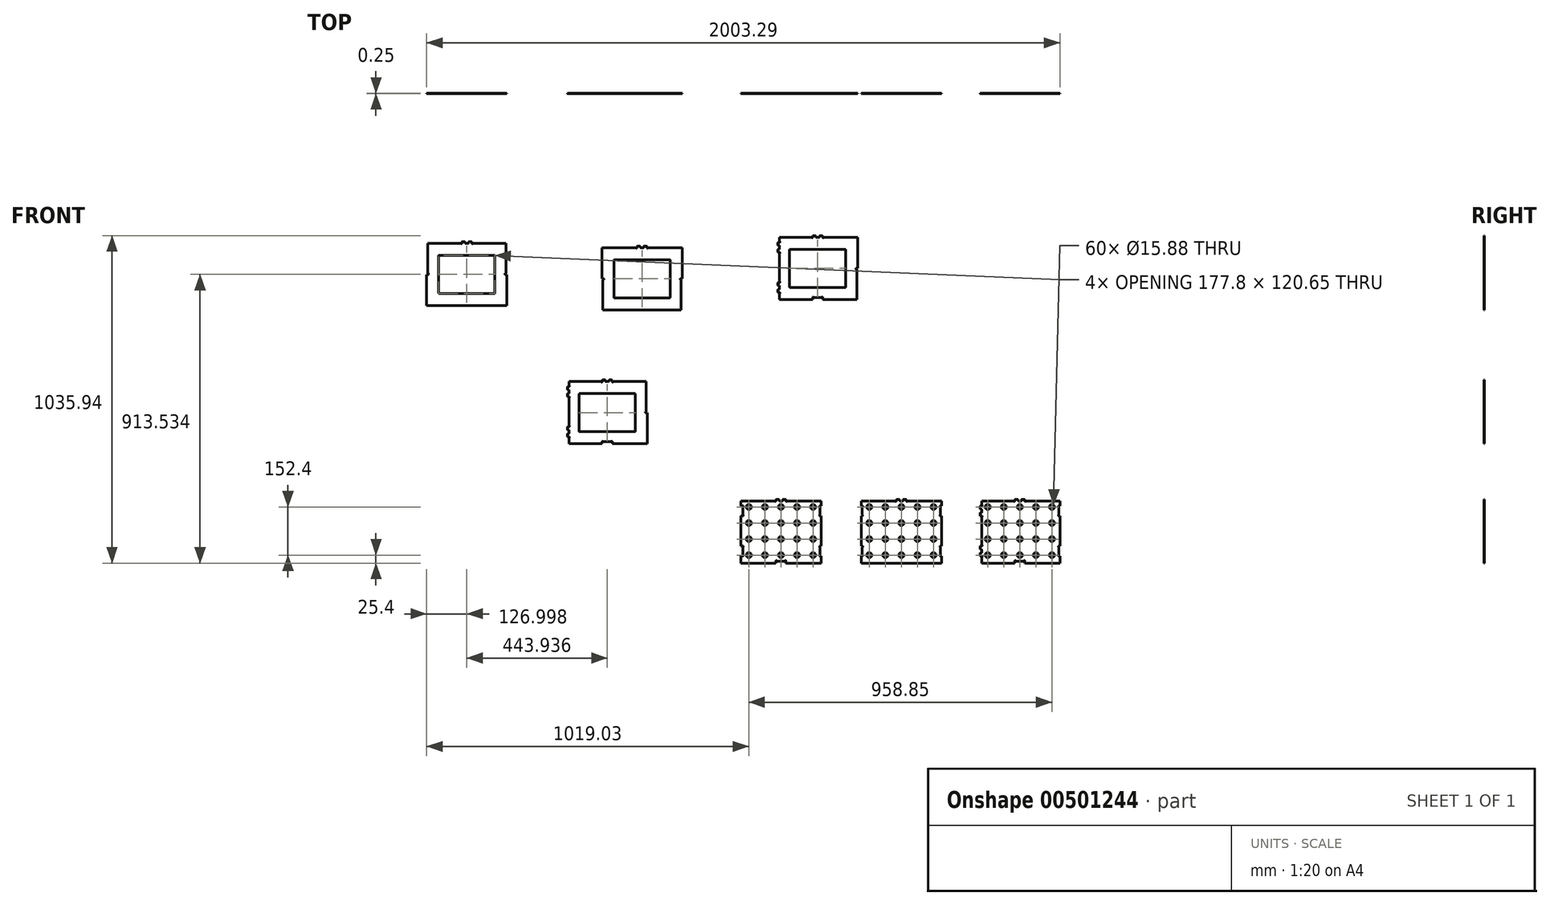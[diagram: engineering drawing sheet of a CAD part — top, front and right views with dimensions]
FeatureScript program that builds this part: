
annotation { "Feature Type Name" : "Feature", "Feature Type Description" : "" }
export const myFeature = defineFeature(function(context is Context, id is Id, definition is map)
    precondition{}
    {
        {
            assignVariable(context, id + "F0", {"name" : "TopPlateThickness", "anyValue" : 0.25});
        }
        {
            assignVariable(context, id + "F1", {"name" : "XMemberThickness", "anyValue" : 0.25});
        }
        {
            var Q0;
            Q0=qCreatedBy(makeId("Front.planeOp"),FACE);
            var sketch = newSketch(context, id + "F2", { "sketchPlane" : qUnion([Q0])});
            skLineSegment(sketch, "E0.MirrorCS", {"start": v(-827.8, -356.83) * mm, "end": v(-827.7, -363.3) * mm});
            skLineSegment(sketch, "E1", {"start": v(-795.8, -356.31) * mm, "end": v(-795.7, -362.8) * mm});
            skArc(sketch, "E2", {"start": v(-824.86, -355.99) * mm, "mid": v(-826.66, -355.28) * mm, "end": v(-827.8, -356.83) * mm});
            skArc(sketch, "E3", {"start": v(-824.86, -355.99) * mm, "mid": v(-824.27, -356.56) * mm, "end": v(-823.47, -356.76) * mm});
            skArc(sketch, "E4.MirrorCS", {"start": v(-798.78, -355.57) * mm, "mid": v(-797, -354.8) * mm, "end": v(-795.8, -356.31) * mm});
            skArc(sketch, "E5.MirrorCS", {"start": v(-798.78, -355.57) * mm, "mid": v(-799.35, -356.16) * mm, "end": v(-800.15, -356.38) * mm});
            skLineSegment(sketch, "E6.trimOffspring", {"start": v(-800.15, -356.38) * mm, "end": v(-823.47, -356.76) * mm});
            skLineSegment(sketch, "E7", {"start": v(-827.8, -356.83) * mm, "end": v(-823.47, -356.76) * mm, "construction": true});
            skLineSegment(sketch, "E8", {"start": v(-800.15, -356.38) * mm, "end": v(-795.8, -356.31) * mm, "construction": true});
            skLineSegment(sketch, "E9", {"start": v(-811.8, -356.57) * mm, "end": v(-811.7, -363.05) * mm, "construction": true});
            skLineSegment(sketch, "E10", {"start": v(-827.7, -363.3) * mm, "end": v(-811.7, -363.05) * mm, "construction": true});
            skLineSegment(sketch, "E11.left", {"start": v(-825.35, -397.01) * mm, "end": v(-825.13, -400.5) * mm});
            skLineSegment(sketch, "E12", {"start": v(-823.86, -395.33) * mm, "end": v(-817.27, -394.91) * mm});
            skArc(sketch, "E13.filletArc", {"start": v(-823.86, -395.33) * mm, "mid": v(-824.96, -395.86) * mm, "end": v(-825.35, -397.01) * mm});
            skLineSegment(sketch, "E14", {"start": v(-813.79, -399.78) * mm, "end": v(-809.54, -399.51) * mm});
            skLineSegment(sketch, "E15.MirrorCS", {"start": v(-794.17, -395.05) * mm, "end": v(-793.95, -398.53) * mm});
            skLineSegment(sketch, "E16.MirrorCS", {"start": v(-795.85, -393.56) * mm, "end": v(-802.44, -393.98) * mm});
            skArc(sketch, "E17.MirrorCS", {"start": v(-795.85, -393.56) * mm, "mid": v(-794.7, -393.96) * mm, "end": v(-794.17, -395.05) * mm});
            skArc(sketch, "E18", {"start": v(-815.59, -396.4) * mm, "mid": v(-816.12, -395.3) * mm, "end": v(-817.27, -394.91) * mm});
            skArc(sketch, "E19", {"start": v(-815.47, -398.3) * mm, "mid": v(-814.93, -399.39) * mm, "end": v(-813.79, -399.78) * mm});
            skArc(sketch, "E20", {"start": v(-805.3, -399.25) * mm, "mid": v(-804.2, -398.71) * mm, "end": v(-803.8, -397.56) * mm});
            skArc(sketch, "E21", {"start": v(-802.44, -393.98) * mm, "mid": v(-803.53, -394.51) * mm, "end": v(-803.93, -395.66) * mm});
            skLineSegment(sketch, "E22", {"start": v(-805.3, -399.25) * mm, "end": v(-809.54, -399.51) * mm});
            skArc(sketch, "E23", {"start": v(-828.3, -400.7) * mm, "mid": v(-826.61, -402.18) * mm, "end": v(-825.13, -400.5) * mm});
            skArc(sketch, "E24", {"start": v(-793.95, -398.53) * mm, "mid": v(-792.27, -400.02) * mm, "end": v(-790.78, -398.33) * mm});
            skLineSegment(sketch, "E25.0", {"start": v(-825.13, -400.5) * mm, "end": v(-793.95, -398.53) * mm, "construction": true});
            skLineSegment(sketch, "E26.0", {"start": v(-817.17, -396.5) * mm, "end": v(-802.34, -395.56) * mm, "construction": true});
            skLineSegment(sketch, "E27.0", {"start": v(-823.86, -395.33) * mm, "end": v(-795.85, -393.56) * mm, "construction": true});
            skLineSegment(sketch, "E28", {"start": v(-823.86, -395.33) * mm, "end": v(-823.55, -400.4) * mm, "construction": true});
            skLineSegment(sketch, "E29", {"start": v(-815.59, -396.4) * mm, "end": v(-815.47, -398.3) * mm});
            skLineSegment(sketch, "E30", {"start": v(-803.93, -395.66) * mm, "end": v(-803.8, -397.56) * mm});
            skLineSegment(sketch, "E31.bottom", {"start": v(-215.61, 91.96) * mm, "end": v(-113.76, 91.96) * mm});
            skLineSegment(sketch, "E31.top", {"start": v(-215.61, -104.9) * mm, "end": v(32.04, -104.9) * mm});
            skLineSegment(sketch, "E31.left", {"start": v(-215.61, 91.96) * mm, "end": v(-215.61, 79) * mm});
            skLineSegment(sketch, "E31.right", {"start": v(32.04, 91.96) * mm, "end": v(32.04, -104.9) * mm});
            skLineSegment(sketch, "E32", {"start": v(-215.61, 72.9) * mm, "end": v(-196.56, 72.9) * mm, "construction": true});
            skLineSegment(sketch, "E33", {"start": v(-196.56, 72.9) * mm, "end": v(-196.56, 91.96) * mm, "construction": true});
            skCircle(sketch, "E34", {"center": v(-196.56, 72.9) * mm, "radius": 7.94 * mm});
            skCircle(sketch, "E35.0.1.0", {"center": v(-196.56, 22.1) * mm, "radius": 7.94 * mm});
            skCircle(sketch, "E35.0.2.0", {"center": v(-196.56, -28.7) * mm, "radius": 7.94 * mm});
            skCircle(sketch, "E35.0.3.0", {"center": v(-196.56, -79.5) * mm, "radius": 7.94 * mm});
            skCircle(sketch, "E35.1.0.0", {"center": v(-145.76, 72.9) * mm, "radius": 7.94 * mm});
            skCircle(sketch, "E35.1.1.0", {"center": v(-145.76, 22.1) * mm, "radius": 7.94 * mm});
            skCircle(sketch, "E35.1.2.0", {"center": v(-145.76, -28.7) * mm, "radius": 7.94 * mm});
            skCircle(sketch, "E35.1.3.0", {"center": v(-145.76, -79.5) * mm, "radius": 7.94 * mm});
            skCircle(sketch, "E35.2.0.0", {"center": v(-94.96, 72.9) * mm, "radius": 7.94 * mm});
            skCircle(sketch, "E35.2.1.0", {"center": v(-94.96, 22.1) * mm, "radius": 7.94 * mm});
            skCircle(sketch, "E35.2.2.0", {"center": v(-94.96, -28.7) * mm, "radius": 7.94 * mm});
            skCircle(sketch, "E35.2.3.0", {"center": v(-94.96, -79.5) * mm, "radius": 7.94 * mm});
            skCircle(sketch, "E35.3.0.0", {"center": v(-44.16, 72.9) * mm, "radius": 7.94 * mm});
            skCircle(sketch, "E35.3.1.0", {"center": v(-44.16, 22.1) * mm, "radius": 7.94 * mm});
            skCircle(sketch, "E35.3.2.0", {"center": v(-44.16, -28.7) * mm, "radius": 7.94 * mm});
            skCircle(sketch, "E35.3.3.0", {"center": v(-44.16, -79.5) * mm, "radius": 7.94 * mm});
            skCircle(sketch, "E35.4.0.0", {"center": v(6.64, 72.9) * mm, "radius": 7.94 * mm});
            skCircle(sketch, "E35.4.1.0", {"center": v(6.64, 22.1) * mm, "radius": 7.94 * mm});
            skCircle(sketch, "E35.4.2.0", {"center": v(6.64, -28.7) * mm, "radius": 7.94 * mm});
            skCircle(sketch, "E35.4.3.0", {"center": v(6.64, -79.5) * mm, "radius": 7.94 * mm});
            skLineSegment(sketch, "E35.direction1", {"start": v(-196.56, 72.9) * mm, "end": v(-145.76, 72.9) * mm, "construction": true});
            skLineSegment(sketch, "E35.direction2", {"start": v(-196.56, 72.9) * mm, "end": v(-196.56, 22.1) * mm, "construction": true});
            skLineSegment(sketch, "E36.MirrorCS", {"start": v(-110.97, -98.41) * mm, "end": v(-110.97, -104.9) * mm});
            skLineSegment(sketch, "E37", {"start": v(-78.96, -98.41) * mm, "end": v(-78.96, -104.9) * mm});
            skArc(sketch, "E38", {"start": v(-108, -97.62) * mm, "mid": v(-109.8, -96.88) * mm, "end": v(-110.97, -98.41) * mm});
            skArc(sketch, "E39", {"start": v(-108, -97.62) * mm, "mid": v(-107.42, -98.2) * mm, "end": v(-106.63, -98.41) * mm});
            skArc(sketch, "E40.MirrorCS", {"start": v(-81.93, -97.62) * mm, "mid": v(-80.14, -96.88) * mm, "end": v(-78.96, -98.41) * mm});
            skArc(sketch, "E41.MirrorCS", {"start": v(-81.93, -97.62) * mm, "mid": v(-82.5, -98.2) * mm, "end": v(-83.3, -98.41) * mm});
            skLineSegment(sketch, "E42.trimOffspring", {"start": v(-83.3, -98.41) * mm, "end": v(-106.63, -98.41) * mm});
            skLineSegment(sketch, "E43", {"start": v(-110.97, -98.41) * mm, "end": v(-106.63, -98.41) * mm, "construction": true});
            skLineSegment(sketch, "E44", {"start": v(-83.3, -98.41) * mm, "end": v(-78.96, -98.41) * mm, "construction": true});
            skLineSegment(sketch, "E45", {"start": v(-94.96, -98.41) * mm, "end": v(-94.96, -104.9) * mm, "construction": true});
            skLineSegment(sketch, "E46", {"start": v(-110.97, -104.9) * mm, "end": v(-94.96, -104.9) * mm, "construction": true});
            skLineSegment(sketch, "E47.MirrorCS", {"start": v(28.8, 44.2) * mm, "end": v(32.04, 44.2) * mm});
            skLineSegment(sketch, "E48", {"start": v(28.8, 76.21) * mm, "end": v(32.04, 76.21) * mm});
            skArc(sketch, "E49", {"start": v(28, 47.17) * mm, "mid": v(27.26, 45.38) * mm, "end": v(28.8, 44.2) * mm});
            skArc(sketch, "E50", {"start": v(28, 47.17) * mm, "mid": v(28.58, 47.75) * mm, "end": v(28.8, 48.55) * mm});
            skArc(sketch, "E51.MirrorCS", {"start": v(28, 73.25) * mm, "mid": v(27.26, 75.04) * mm, "end": v(28.8, 76.21) * mm});
            skArc(sketch, "E52.MirrorCS", {"start": v(28, 73.25) * mm, "mid": v(28.58, 72.67) * mm, "end": v(28.8, 71.87) * mm});
            skLineSegment(sketch, "E53.trimOffspring", {"start": v(28.8, 71.87) * mm, "end": v(28.8, 48.55) * mm});
            skLineSegment(sketch, "E54", {"start": v(28.8, 44.2) * mm, "end": v(28.8, 48.55) * mm, "construction": true});
            skLineSegment(sketch, "E55", {"start": v(28.8, 71.87) * mm, "end": v(28.8, 76.21) * mm, "construction": true});
            skLineSegment(sketch, "E56", {"start": v(28.8, 60.2) * mm, "end": v(32.04, 60.2) * mm, "construction": true});
            skLineSegment(sketch, "E57", {"start": v(32.04, 44.2) * mm, "end": v(32.04, 60.2) * mm, "construction": true});
            skLineSegment(sketch, "E58.MirrorCS", {"start": v(28.8, -82.8) * mm, "end": v(32.04, -82.8) * mm});
            skLineSegment(sketch, "E59", {"start": v(28.8, -50.79) * mm, "end": v(32.04, -50.79) * mm});
            skArc(sketch, "E60", {"start": v(28, -79.83) * mm, "mid": v(27.26, -81.62) * mm, "end": v(28.8, -82.8) * mm});
            skArc(sketch, "E61", {"start": v(28, -79.83) * mm, "mid": v(28.58, -79.25) * mm, "end": v(28.8, -78.45) * mm});
            skArc(sketch, "E62.MirrorCS", {"start": v(28, -53.75) * mm, "mid": v(27.26, -51.96) * mm, "end": v(28.8, -50.79) * mm});
            skArc(sketch, "E63.MirrorCS", {"start": v(28, -53.75) * mm, "mid": v(28.58, -54.33) * mm, "end": v(28.8, -55.13) * mm});
            skLineSegment(sketch, "E64.trimOffspring", {"start": v(28.8, -55.13) * mm, "end": v(28.8, -78.45) * mm});
            skLineSegment(sketch, "E65", {"start": v(28.8, -82.8) * mm, "end": v(28.8, -78.45) * mm, "construction": true});
            skLineSegment(sketch, "E66", {"start": v(28.8, -55.13) * mm, "end": v(28.8, -50.79) * mm, "construction": true});
            skLineSegment(sketch, "E67", {"start": v(28.8, -66.8) * mm, "end": v(32.04, -66.8) * mm, "construction": true});
            skLineSegment(sketch, "E68", {"start": v(32.04, -82.8) * mm, "end": v(32.04, -66.8) * mm, "construction": true});
            skLineSegment(sketch, "E69.left", {"start": v(-219.1, 44.59) * mm, "end": v(-215.61, 44.59) * mm});
            skLineSegment(sketch, "E70", {"start": v(-220.7, 46.18) * mm, "end": v(-220.7, 52.78) * mm});
            skArc(sketch, "E71.filletArc", {"start": v(-220.7, 46.18) * mm, "mid": v(-220.23, 45.05) * mm, "end": v(-219.1, 44.59) * mm});
            skLineSegment(sketch, "E72", {"start": v(-215.61, 55.96) * mm, "end": v(-215.61, 60.2) * mm});
            skLineSegment(sketch, "E73.MirrorCS", {"start": v(-219.1, 75.83) * mm, "end": v(-215.61, 75.83) * mm});
            skLineSegment(sketch, "E74.MirrorCS", {"start": v(-220.7, 74.24) * mm, "end": v(-220.7, 67.64) * mm});
            skArc(sketch, "E75.MirrorCS", {"start": v(-220.7, 74.24) * mm, "mid": v(-220.23, 75.37) * mm, "end": v(-219.1, 75.83) * mm});
            skArc(sketch, "E76", {"start": v(-219.1, 54.37) * mm, "mid": v(-220.23, 53.9) * mm, "end": v(-220.7, 52.78) * mm});
            skArc(sketch, "E77", {"start": v(-217.2, 54.37) * mm, "mid": v(-216.08, 54.83) * mm, "end": v(-215.61, 55.96) * mm});
            skArc(sketch, "E78", {"start": v(-215.61, 64.46) * mm, "mid": v(-216.08, 65.59) * mm, "end": v(-217.2, 66.05) * mm});
            skArc(sketch, "E79", {"start": v(-220.7, 67.64) * mm, "mid": v(-220.23, 66.52) * mm, "end": v(-219.1, 66.05) * mm});
            skLineSegment(sketch, "E80", {"start": v(-215.61, 64.46) * mm, "end": v(-215.61, 60.2) * mm});
            skArc(sketch, "E81", {"start": v(-215.61, 41.41) * mm, "mid": v(-214.03, 43) * mm, "end": v(-215.61, 44.59) * mm});
            skArc(sketch, "E82", {"start": v(-215.61, 75.83) * mm, "mid": v(-214.03, 77.42) * mm, "end": v(-215.61, 79) * mm});
            skLineSegment(sketch, "E83.0", {"start": v(-219.1, 52.78) * mm, "end": v(-219.1, 67.64) * mm, "construction": true});
            skLineSegment(sketch, "E84.0", {"start": v(-220.7, 46.18) * mm, "end": v(-220.7, 74.24) * mm, "construction": true});
            skLineSegment(sketch, "E85", {"start": v(-215.61, 46.18) * mm, "end": v(-220.7, 46.18) * mm, "construction": true});
            skLineSegment(sketch, "E86", {"start": v(-219.1, 54.37) * mm, "end": v(-217.2, 54.37) * mm});
            skLineSegment(sketch, "E87", {"start": v(-219.1, 66.05) * mm, "end": v(-217.2, 66.05) * mm});
            skLineSegment(sketch, "E88.left", {"start": v(-219.1, -82.41) * mm, "end": v(-215.61, -82.41) * mm});
            skLineSegment(sketch, "E89", {"start": v(-220.7, -80.82) * mm, "end": v(-220.7, -74.22) * mm});
            skArc(sketch, "E90.filletArc", {"start": v(-220.7, -80.82) * mm, "mid": v(-220.23, -81.95) * mm, "end": v(-219.1, -82.41) * mm});
            skLineSegment(sketch, "E91", {"start": v(-215.61, -71.04) * mm, "end": v(-215.61, -66.8) * mm});
            skLineSegment(sketch, "E92.MirrorCS", {"start": v(-219.1, -51.17) * mm, "end": v(-215.61, -51.17) * mm});
            skLineSegment(sketch, "E93.MirrorCS", {"start": v(-220.7, -52.76) * mm, "end": v(-220.7, -59.36) * mm});
            skArc(sketch, "E94.MirrorCS", {"start": v(-220.7, -52.76) * mm, "mid": v(-220.23, -51.63) * mm, "end": v(-219.1, -51.17) * mm});
            skArc(sketch, "E95", {"start": v(-219.1, -72.63) * mm, "mid": v(-220.23, -73.1) * mm, "end": v(-220.7, -74.22) * mm});
            skArc(sketch, "E96", {"start": v(-217.2, -72.63) * mm, "mid": v(-216.08, -72.17) * mm, "end": v(-215.61, -71.04) * mm});
            skArc(sketch, "E97", {"start": v(-215.61, -62.54) * mm, "mid": v(-216.08, -61.41) * mm, "end": v(-217.2, -60.95) * mm});
            skArc(sketch, "E98", {"start": v(-220.7, -59.36) * mm, "mid": v(-220.23, -60.48) * mm, "end": v(-219.1, -60.95) * mm});
            skLineSegment(sketch, "E99", {"start": v(-215.61, -62.54) * mm, "end": v(-215.61, -66.8) * mm});
            skArc(sketch, "E100", {"start": v(-215.61, -85.59) * mm, "mid": v(-214.03, -84) * mm, "end": v(-215.61, -82.41) * mm});
            skArc(sketch, "E101", {"start": v(-215.61, -51.17) * mm, "mid": v(-214.03, -49.58) * mm, "end": v(-215.61, -48) * mm});
            skLineSegment(sketch, "E102.0", {"start": v(-219.1, -74.22) * mm, "end": v(-219.1, -59.36) * mm, "construction": true});
            skLineSegment(sketch, "E103.0", {"start": v(-220.7, -80.82) * mm, "end": v(-220.7, -52.76) * mm, "construction": true});
            skLineSegment(sketch, "E104", {"start": v(-220.7, -80.82) * mm, "end": v(-215.61, -80.82) * mm, "construction": true});
            skLineSegment(sketch, "E105", {"start": v(-219.1, -72.63) * mm, "end": v(-217.2, -72.63) * mm});
            skLineSegment(sketch, "E106", {"start": v(-219.1, -60.95) * mm, "end": v(-217.2, -60.95) * mm});
            skLineSegment(sketch, "E107.trimOffspring", {"start": v(-215.61, -85.59) * mm, "end": v(-215.61, -104.9) * mm});
            skLineSegment(sketch, "E108.trimOffspring", {"start": v(-215.61, 41.41) * mm, "end": v(-215.61, -48) * mm});
            skLineSegment(sketch, "E109.left", {"start": v(-110.59, 95.45) * mm, "end": v(-110.59, 91.96) * mm});
            skLineSegment(sketch, "E110", {"start": v(-109, 97.04) * mm, "end": v(-102.4, 97.04) * mm});
            skArc(sketch, "E111.filletArc", {"start": v(-109, 97.04) * mm, "mid": v(-110.12, 96.57) * mm, "end": v(-110.59, 95.45) * mm});
            skLineSegment(sketch, "E112", {"start": v(-99.22, 91.96) * mm, "end": v(-94.96, 91.96) * mm});
            skLineSegment(sketch, "E113.MirrorCS", {"start": v(-79.34, 95.45) * mm, "end": v(-79.34, 91.96) * mm});
            skLineSegment(sketch, "E114.MirrorCS", {"start": v(-80.93, 97.04) * mm, "end": v(-87.54, 97.04) * mm});
            skArc(sketch, "E115.MirrorCS", {"start": v(-80.93, 97.04) * mm, "mid": v(-79.8, 96.57) * mm, "end": v(-79.34, 95.45) * mm});
            skArc(sketch, "E116", {"start": v(-100.8, 95.45) * mm, "mid": v(-101.27, 96.57) * mm, "end": v(-102.4, 97.04) * mm});
            skArc(sketch, "E117", {"start": v(-100.8, 93.55) * mm, "mid": v(-100.34, 92.42) * mm, "end": v(-99.22, 91.96) * mm});
            skArc(sketch, "E118", {"start": v(-90.71, 91.96) * mm, "mid": v(-89.59, 92.42) * mm, "end": v(-89.12, 93.55) * mm});
            skArc(sketch, "E119", {"start": v(-87.54, 97.04) * mm, "mid": v(-88.66, 96.57) * mm, "end": v(-89.12, 95.45) * mm});
            skLineSegment(sketch, "E120", {"start": v(-90.71, 91.96) * mm, "end": v(-94.96, 91.96) * mm});
            skArc(sketch, "E121", {"start": v(-113.76, 91.96) * mm, "mid": v(-112.17, 90.37) * mm, "end": v(-110.59, 91.96) * mm});
            skArc(sketch, "E122", {"start": v(-79.34, 91.96) * mm, "mid": v(-77.76, 90.37) * mm, "end": v(-76.17, 91.96) * mm});
            skLineSegment(sketch, "E123.0", {"start": v(-110.59, 91.96) * mm, "end": v(-79.34, 91.96) * mm, "construction": true});
            skLineSegment(sketch, "E124.0", {"start": v(-102.4, 95.45) * mm, "end": v(-87.54, 95.45) * mm, "construction": true});
            skLineSegment(sketch, "E125.0", {"start": v(-109, 97.04) * mm, "end": v(-80.93, 97.04) * mm, "construction": true});
            skLineSegment(sketch, "E126", {"start": v(-109, 97.04) * mm, "end": v(-109, 91.96) * mm, "construction": true});
            skLineSegment(sketch, "E127", {"start": v(-100.8, 95.45) * mm, "end": v(-100.8, 93.55) * mm});
            skLineSegment(sketch, "E128", {"start": v(-89.12, 95.45) * mm, "end": v(-89.12, 93.55) * mm});
            skLineSegment(sketch, "E129.trimOffspring", {"start": v(-76.17, 91.96) * mm, "end": v(32.04, 91.96) * mm});
            skLineSegment(sketch, "E130.bottom", {"start": v(-977.61, 91.96) * mm, "end": v(-869.41, 91.96) * mm});
            skLineSegment(sketch, "E130.top", {"start": v(-977.61, -104.9) * mm, "end": v(-723.61, -104.9) * mm});
            skLineSegment(sketch, "E130.left", {"start": v(-977.61, 91.96) * mm, "end": v(-977.61, -104.9) * mm});
            skLineSegment(sketch, "E130.right", {"start": v(-723.61, 91.96) * mm, "end": v(-723.61, -104.9) * mm});
            skLineSegment(sketch, "E131", {"start": v(-977.61, 72.9) * mm, "end": v(-952.21, 72.9) * mm, "construction": true});
            skLineSegment(sketch, "E132", {"start": v(-952.21, 72.9) * mm, "end": v(-952.21, 91.96) * mm, "construction": true});
            skCircle(sketch, "E133", {"center": v(-952.21, 72.9) * mm, "radius": 7.94 * mm});
            skCircle(sketch, "E134.0.1.0", {"center": v(-952.21, 22.1) * mm, "radius": 7.94 * mm});
            skCircle(sketch, "E134.0.2.0", {"center": v(-952.21, -28.7) * mm, "radius": 7.94 * mm});
            skCircle(sketch, "E134.0.3.0", {"center": v(-952.21, -79.5) * mm, "radius": 7.94 * mm});
            skCircle(sketch, "E134.1.0.0", {"center": v(-901.41, 72.9) * mm, "radius": 7.94 * mm});
            skCircle(sketch, "E134.1.1.0", {"center": v(-901.41, 22.1) * mm, "radius": 7.94 * mm});
            skCircle(sketch, "E134.1.2.0", {"center": v(-901.41, -28.7) * mm, "radius": 7.94 * mm});
            skCircle(sketch, "E134.1.3.0", {"center": v(-901.41, -79.5) * mm, "radius": 7.94 * mm});
            skCircle(sketch, "E134.2.0.0", {"center": v(-850.61, 72.9) * mm, "radius": 7.94 * mm});
            skCircle(sketch, "E134.2.1.0", {"center": v(-850.61, 22.1) * mm, "radius": 7.94 * mm});
            skCircle(sketch, "E134.2.2.0", {"center": v(-850.61, -28.7) * mm, "radius": 7.94 * mm});
            skCircle(sketch, "E134.2.3.0", {"center": v(-850.61, -79.5) * mm, "radius": 7.94 * mm});
            skCircle(sketch, "E134.3.0.0", {"center": v(-799.81, 72.9) * mm, "radius": 7.94 * mm});
            skCircle(sketch, "E134.3.1.0", {"center": v(-799.81, 22.1) * mm, "radius": 7.94 * mm});
            skCircle(sketch, "E134.3.2.0", {"center": v(-799.81, -28.7) * mm, "radius": 7.94 * mm});
            skCircle(sketch, "E134.3.3.0", {"center": v(-799.81, -79.5) * mm, "radius": 7.94 * mm});
            skCircle(sketch, "E134.4.0.0", {"center": v(-749.01, 72.9) * mm, "radius": 7.94 * mm});
            skCircle(sketch, "E134.4.1.0", {"center": v(-749.01, 22.1) * mm, "radius": 7.94 * mm});
            skCircle(sketch, "E134.4.2.0", {"center": v(-749.01, -28.7) * mm, "radius": 7.94 * mm});
            skCircle(sketch, "E134.4.3.0", {"center": v(-749.01, -79.5) * mm, "radius": 7.94 * mm});
            skLineSegment(sketch, "E134.direction1", {"start": v(-952.21, 72.9) * mm, "end": v(-901.41, 72.9) * mm, "construction": true});
            skLineSegment(sketch, "E134.direction2", {"start": v(-952.21, 72.9) * mm, "end": v(-952.21, 22.1) * mm, "construction": true});
            skLineSegment(sketch, "E135.MirrorCS", {"start": v(-866.62, -98.41) * mm, "end": v(-866.62, -104.9) * mm});
            skLineSegment(sketch, "E136", {"start": v(-834.61, -98.41) * mm, "end": v(-834.61, -104.9) * mm});
            skArc(sketch, "E137", {"start": v(-863.65, -97.62) * mm, "mid": v(-865.44, -96.88) * mm, "end": v(-866.62, -98.41) * mm});
            skArc(sketch, "E138", {"start": v(-863.65, -97.62) * mm, "mid": v(-863.07, -98.2) * mm, "end": v(-862.28, -98.41) * mm});
            skArc(sketch, "E139.MirrorCS", {"start": v(-837.58, -97.62) * mm, "mid": v(-835.79, -96.88) * mm, "end": v(-834.61, -98.41) * mm});
            skArc(sketch, "E140.MirrorCS", {"start": v(-837.58, -97.62) * mm, "mid": v(-838.16, -98.2) * mm, "end": v(-838.95, -98.41) * mm});
            skLineSegment(sketch, "E141.trimOffspring", {"start": v(-838.95, -98.41) * mm, "end": v(-862.28, -98.41) * mm});
            skLineSegment(sketch, "E142", {"start": v(-866.62, -98.41) * mm, "end": v(-862.28, -98.41) * mm, "construction": true});
            skLineSegment(sketch, "E143", {"start": v(-838.95, -98.41) * mm, "end": v(-834.61, -98.41) * mm, "construction": true});
            skLineSegment(sketch, "E144", {"start": v(-850.61, -98.41) * mm, "end": v(-850.61, -104.9) * mm, "construction": true});
            skLineSegment(sketch, "E145", {"start": v(-866.62, -104.9) * mm, "end": v(-850.61, -104.9) * mm, "construction": true});
            skLineSegment(sketch, "E146.MirrorCS", {"start": v(-726.85, 44.2) * mm, "end": v(-723.61, 44.2) * mm});
            skLineSegment(sketch, "E147", {"start": v(-726.85, 76.21) * mm, "end": v(-723.61, 76.21) * mm});
            skArc(sketch, "E148", {"start": v(-727.65, 47.17) * mm, "mid": v(-728.39, 45.38) * mm, "end": v(-726.85, 44.2) * mm});
            skArc(sketch, "E149", {"start": v(-727.65, 47.17) * mm, "mid": v(-727.07, 47.75) * mm, "end": v(-726.85, 48.55) * mm});
            skArc(sketch, "E150.MirrorCS", {"start": v(-727.65, 73.25) * mm, "mid": v(-728.39, 75.04) * mm, "end": v(-726.85, 76.21) * mm});
            skArc(sketch, "E151.MirrorCS", {"start": v(-727.65, 73.25) * mm, "mid": v(-727.07, 72.67) * mm, "end": v(-726.85, 71.87) * mm});
            skLineSegment(sketch, "E152.trimOffspring", {"start": v(-726.85, 71.87) * mm, "end": v(-726.85, 48.55) * mm});
            skLineSegment(sketch, "E153", {"start": v(-726.85, 44.2) * mm, "end": v(-726.85, 48.55) * mm, "construction": true});
            skLineSegment(sketch, "E154", {"start": v(-726.85, 71.87) * mm, "end": v(-726.85, 76.21) * mm, "construction": true});
            skLineSegment(sketch, "E155", {"start": v(-726.85, 60.2) * mm, "end": v(-723.61, 60.2) * mm, "construction": true});
            skLineSegment(sketch, "E156", {"start": v(-723.61, 44.2) * mm, "end": v(-723.61, 60.2) * mm, "construction": true});
            skLineSegment(sketch, "E157.MirrorCS", {"start": v(-726.85, -82.8) * mm, "end": v(-723.61, -82.8) * mm});
            skLineSegment(sketch, "E158", {"start": v(-726.85, -50.79) * mm, "end": v(-723.61, -50.79) * mm});
            skArc(sketch, "E159", {"start": v(-727.65, -79.83) * mm, "mid": v(-728.39, -81.62) * mm, "end": v(-726.85, -82.8) * mm});
            skArc(sketch, "E160", {"start": v(-727.65, -79.83) * mm, "mid": v(-727.07, -79.25) * mm, "end": v(-726.85, -78.45) * mm});
            skArc(sketch, "E161.MirrorCS", {"start": v(-727.65, -53.75) * mm, "mid": v(-728.39, -51.96) * mm, "end": v(-726.85, -50.79) * mm});
            skArc(sketch, "E162.MirrorCS", {"start": v(-727.65, -53.75) * mm, "mid": v(-727.07, -54.33) * mm, "end": v(-726.85, -55.13) * mm});
            skLineSegment(sketch, "E163.trimOffspring", {"start": v(-726.85, -55.13) * mm, "end": v(-726.85, -78.45) * mm});
            skLineSegment(sketch, "E164", {"start": v(-726.85, -82.8) * mm, "end": v(-726.85, -78.45) * mm, "construction": true});
            skLineSegment(sketch, "E165", {"start": v(-726.85, -55.13) * mm, "end": v(-726.85, -50.79) * mm, "construction": true});
            skLineSegment(sketch, "E166", {"start": v(-726.85, -66.8) * mm, "end": v(-723.61, -66.8) * mm, "construction": true});
            skLineSegment(sketch, "E167", {"start": v(-723.61, -82.8) * mm, "end": v(-723.61, -66.8) * mm, "construction": true});
            skLineSegment(sketch, "E168.left", {"start": v(-866.24, 95.45) * mm, "end": v(-866.24, 91.96) * mm});
            skLineSegment(sketch, "E169", {"start": v(-864.65, 97.04) * mm, "end": v(-858.04, 97.04) * mm});
            skArc(sketch, "E170.filletArc", {"start": v(-864.65, 97.04) * mm, "mid": v(-865.77, 96.57) * mm, "end": v(-866.24, 95.45) * mm});
            skLineSegment(sketch, "E171", {"start": v(-854.87, 91.96) * mm, "end": v(-850.61, 91.96) * mm});
            skLineSegment(sketch, "E172.MirrorCS", {"start": v(-835, 95.45) * mm, "end": v(-835, 91.96) * mm});
            skLineSegment(sketch, "E173.MirrorCS", {"start": v(-836.58, 97.04) * mm, "end": v(-843.19, 97.04) * mm});
            skArc(sketch, "E174.MirrorCS", {"start": v(-836.58, 97.04) * mm, "mid": v(-835.46, 96.57) * mm, "end": v(-835, 95.45) * mm});
            skArc(sketch, "E175", {"start": v(-856.46, 95.45) * mm, "mid": v(-856.92, 96.57) * mm, "end": v(-858.04, 97.04) * mm});
            skArc(sketch, "E176", {"start": v(-856.46, 93.55) * mm, "mid": v(-856, 92.42) * mm, "end": v(-854.87, 91.96) * mm});
            skArc(sketch, "E177", {"start": v(-846.36, 91.96) * mm, "mid": v(-845.24, 92.42) * mm, "end": v(-844.77, 93.55) * mm});
            skArc(sketch, "E178", {"start": v(-843.19, 97.04) * mm, "mid": v(-844.3, 96.57) * mm, "end": v(-844.77, 95.45) * mm});
            skLineSegment(sketch, "E179", {"start": v(-846.36, 91.96) * mm, "end": v(-850.61, 91.96) * mm});
            skArc(sketch, "E180", {"start": v(-869.41, 91.96) * mm, "mid": v(-867.82, 90.37) * mm, "end": v(-866.24, 91.96) * mm});
            skArc(sketch, "E181", {"start": v(-835, 91.96) * mm, "mid": v(-833.4, 90.37) * mm, "end": v(-831.82, 91.96) * mm});
            skLineSegment(sketch, "E182.0", {"start": v(-866.24, 91.96) * mm, "end": v(-835, 91.96) * mm, "construction": true});
            skLineSegment(sketch, "E183.0", {"start": v(-858.04, 95.45) * mm, "end": v(-843.19, 95.45) * mm, "construction": true});
            skLineSegment(sketch, "E184.0", {"start": v(-864.65, 97.04) * mm, "end": v(-836.58, 97.04) * mm, "construction": true});
            skLineSegment(sketch, "E185", {"start": v(-864.65, 97.04) * mm, "end": v(-864.65, 91.96) * mm, "construction": true});
            skLineSegment(sketch, "E186", {"start": v(-856.46, 95.45) * mm, "end": v(-856.46, 93.55) * mm});
            skLineSegment(sketch, "E187", {"start": v(-844.77, 95.45) * mm, "end": v(-844.77, 93.55) * mm});
            skLineSegment(sketch, "E188.trimOffspring", {"start": v(-831.82, 91.96) * mm, "end": v(-723.61, 91.96) * mm});
            skLineSegment(sketch, "E189.MirrorCS", {"start": v(-971.14, 76.21) * mm, "end": v(-977.61, 76.21) * mm});
            skLineSegment(sketch, "E190", {"start": v(-971.14, 44.2) * mm, "end": v(-977.61, 44.2) * mm});
            skArc(sketch, "E191", {"start": v(-970.34, 73.25) * mm, "mid": v(-969.6, 75.04) * mm, "end": v(-971.14, 76.21) * mm});
            skArc(sketch, "E192", {"start": v(-970.34, 73.25) * mm, "mid": v(-970.93, 72.67) * mm, "end": v(-971.14, 71.87) * mm});
            skArc(sketch, "E193.MirrorCS", {"start": v(-970.34, 47.17) * mm, "mid": v(-969.6, 45.38) * mm, "end": v(-971.14, 44.2) * mm});
            skArc(sketch, "E194.MirrorCS", {"start": v(-970.34, 47.17) * mm, "mid": v(-970.93, 47.75) * mm, "end": v(-971.14, 48.55) * mm});
            skLineSegment(sketch, "E195.trimOffspring", {"start": v(-971.14, 48.55) * mm, "end": v(-971.14, 71.87) * mm});
            skLineSegment(sketch, "E196", {"start": v(-971.14, 76.21) * mm, "end": v(-971.14, 71.87) * mm, "construction": true});
            skLineSegment(sketch, "E197", {"start": v(-971.14, 48.55) * mm, "end": v(-971.14, 44.2) * mm, "construction": true});
            skLineSegment(sketch, "E198", {"start": v(-971.14, 60.2) * mm, "end": v(-977.61, 60.2) * mm, "construction": true});
            skLineSegment(sketch, "E199", {"start": v(-977.61, 76.21) * mm, "end": v(-977.61, 60.2) * mm, "construction": true});
            skLineSegment(sketch, "E200.MirrorCS", {"start": v(-971.14, -50.79) * mm, "end": v(-977.61, -50.79) * mm});
            skLineSegment(sketch, "E201", {"start": v(-971.14, -82.8) * mm, "end": v(-977.61, -82.8) * mm});
            skArc(sketch, "E202", {"start": v(-970.34, -53.75) * mm, "mid": v(-969.6, -51.96) * mm, "end": v(-971.14, -50.79) * mm});
            skArc(sketch, "E203", {"start": v(-970.34, -53.75) * mm, "mid": v(-970.93, -54.33) * mm, "end": v(-971.14, -55.13) * mm});
            skArc(sketch, "E204.MirrorCS", {"start": v(-970.34, -79.83) * mm, "mid": v(-969.6, -81.62) * mm, "end": v(-971.14, -82.8) * mm});
            skArc(sketch, "E205.MirrorCS", {"start": v(-970.34, -79.83) * mm, "mid": v(-970.93, -79.25) * mm, "end": v(-971.14, -78.45) * mm});
            skLineSegment(sketch, "E206.trimOffspring", {"start": v(-971.14, -78.45) * mm, "end": v(-971.14, -55.13) * mm});
            skLineSegment(sketch, "E207", {"start": v(-971.14, -50.79) * mm, "end": v(-971.14, -55.13) * mm, "construction": true});
            skLineSegment(sketch, "E208", {"start": v(-971.14, -78.45) * mm, "end": v(-971.14, -82.8) * mm, "construction": true});
            skLineSegment(sketch, "E209", {"start": v(-971.14, -66.8) * mm, "end": v(-977.61, -66.8) * mm, "construction": true});
            skLineSegment(sketch, "E210", {"start": v(-977.61, -50.79) * mm, "end": v(-977.61, -66.8) * mm, "construction": true});
            skLineSegment(sketch, "E211.bottom", {"start": v(-596.61, 91.96) * mm, "end": v(-488.41, 91.96) * mm});
            skLineSegment(sketch, "E211.top", {"start": v(-596.61, -104.9) * mm, "end": v(-342.61, -104.9) * mm});
            skLineSegment(sketch, "E211.left", {"start": v(-596.61, 91.96) * mm, "end": v(-596.61, -104.9) * mm});
            skLineSegment(sketch, "E211.right", {"start": v(-342.61, 91.96) * mm, "end": v(-342.61, -104.9) * mm});
            skLineSegment(sketch, "E212", {"start": v(-596.61, 72.9) * mm, "end": v(-571.21, 72.9) * mm, "construction": true});
            skLineSegment(sketch, "E213", {"start": v(-571.21, 72.9) * mm, "end": v(-571.21, 91.96) * mm, "construction": true});
            skCircle(sketch, "E214", {"center": v(-571.21, 72.9) * mm, "radius": 7.94 * mm});
            skCircle(sketch, "E215.0.1.0", {"center": v(-571.21, 22.1) * mm, "radius": 7.94 * mm});
            skCircle(sketch, "E215.0.2.0", {"center": v(-571.21, -28.7) * mm, "radius": 7.94 * mm});
            skCircle(sketch, "E215.0.3.0", {"center": v(-571.21, -79.5) * mm, "radius": 7.94 * mm});
            skCircle(sketch, "E215.1.0.0", {"center": v(-520.41, 72.9) * mm, "radius": 7.94 * mm});
            skCircle(sketch, "E215.1.1.0", {"center": v(-520.41, 22.1) * mm, "radius": 7.94 * mm});
            skCircle(sketch, "E215.1.2.0", {"center": v(-520.41, -28.7) * mm, "radius": 7.94 * mm});
            skCircle(sketch, "E215.1.3.0", {"center": v(-520.41, -79.5) * mm, "radius": 7.94 * mm});
            skCircle(sketch, "E215.2.0.0", {"center": v(-469.61, 72.9) * mm, "radius": 7.94 * mm});
            skCircle(sketch, "E215.2.1.0", {"center": v(-469.61, 22.1) * mm, "radius": 7.94 * mm});
            skCircle(sketch, "E215.2.2.0", {"center": v(-469.61, -28.7) * mm, "radius": 7.94 * mm});
            skCircle(sketch, "E215.2.3.0", {"center": v(-469.61, -79.5) * mm, "radius": 7.94 * mm});
            skCircle(sketch, "E215.3.0.0", {"center": v(-418.81, 72.9) * mm, "radius": 7.94 * mm});
            skCircle(sketch, "E215.3.1.0", {"center": v(-418.81, 22.1) * mm, "radius": 7.94 * mm});
            skCircle(sketch, "E215.3.2.0", {"center": v(-418.81, -28.7) * mm, "radius": 7.94 * mm});
            skCircle(sketch, "E215.3.3.0", {"center": v(-418.81, -79.5) * mm, "radius": 7.94 * mm});
            skCircle(sketch, "E215.4.0.0", {"center": v(-368.01, 72.9) * mm, "radius": 7.94 * mm});
            skCircle(sketch, "E215.4.1.0", {"center": v(-368.01, 22.1) * mm, "radius": 7.94 * mm});
            skCircle(sketch, "E215.4.2.0", {"center": v(-368.01, -28.7) * mm, "radius": 7.94 * mm});
            skCircle(sketch, "E215.4.3.0", {"center": v(-368.01, -79.5) * mm, "radius": 7.94 * mm});
            skLineSegment(sketch, "E215.direction1", {"start": v(-571.21, 72.9) * mm, "end": v(-520.41, 72.9) * mm, "construction": true});
            skLineSegment(sketch, "E215.direction2", {"start": v(-571.21, 72.9) * mm, "end": v(-571.21, 22.1) * mm, "construction": true});
            skLineSegment(sketch, "E216.MirrorCS", {"start": v(-345.85, 44.2) * mm, "end": v(-342.61, 44.2) * mm});
            skLineSegment(sketch, "E217", {"start": v(-345.85, 76.21) * mm, "end": v(-342.61, 76.21) * mm});
            skArc(sketch, "E218", {"start": v(-346.65, 47.17) * mm, "mid": v(-347.39, 45.38) * mm, "end": v(-345.85, 44.2) * mm});
            skArc(sketch, "E219", {"start": v(-346.65, 47.17) * mm, "mid": v(-346.07, 47.75) * mm, "end": v(-345.85, 48.55) * mm});
            skArc(sketch, "E220.MirrorCS", {"start": v(-346.65, 73.25) * mm, "mid": v(-347.39, 75.04) * mm, "end": v(-345.85, 76.21) * mm});
            skArc(sketch, "E221.MirrorCS", {"start": v(-346.65, 73.25) * mm, "mid": v(-346.07, 72.67) * mm, "end": v(-345.85, 71.87) * mm});
            skLineSegment(sketch, "E222.trimOffspring", {"start": v(-345.85, 71.87) * mm, "end": v(-345.85, 48.55) * mm});
            skLineSegment(sketch, "E223", {"start": v(-345.85, 44.2) * mm, "end": v(-345.85, 48.55) * mm, "construction": true});
            skLineSegment(sketch, "E224", {"start": v(-345.85, 71.87) * mm, "end": v(-345.85, 76.21) * mm, "construction": true});
            skLineSegment(sketch, "E225", {"start": v(-345.85, 60.2) * mm, "end": v(-342.61, 60.2) * mm, "construction": true});
            skLineSegment(sketch, "E226", {"start": v(-342.61, 44.2) * mm, "end": v(-342.61, 60.2) * mm, "construction": true});
            skLineSegment(sketch, "E227.MirrorCS", {"start": v(-345.85, -82.8) * mm, "end": v(-342.61, -82.8) * mm});
            skLineSegment(sketch, "E228", {"start": v(-345.85, -50.79) * mm, "end": v(-342.61, -50.79) * mm});
            skArc(sketch, "E229", {"start": v(-346.65, -79.83) * mm, "mid": v(-347.39, -81.62) * mm, "end": v(-345.85, -82.8) * mm});
            skArc(sketch, "E230", {"start": v(-346.65, -79.83) * mm, "mid": v(-346.07, -79.25) * mm, "end": v(-345.85, -78.45) * mm});
            skArc(sketch, "E231.MirrorCS", {"start": v(-346.65, -53.75) * mm, "mid": v(-347.39, -51.96) * mm, "end": v(-345.85, -50.79) * mm});
            skArc(sketch, "E232.MirrorCS", {"start": v(-346.65, -53.75) * mm, "mid": v(-346.07, -54.33) * mm, "end": v(-345.85, -55.13) * mm});
            skLineSegment(sketch, "E233.trimOffspring", {"start": v(-345.85, -55.13) * mm, "end": v(-345.85, -78.45) * mm});
            skLineSegment(sketch, "E234", {"start": v(-345.85, -82.8) * mm, "end": v(-345.85, -78.45) * mm, "construction": true});
            skLineSegment(sketch, "E235", {"start": v(-345.85, -55.13) * mm, "end": v(-345.85, -50.79) * mm, "construction": true});
            skLineSegment(sketch, "E236", {"start": v(-345.85, -66.8) * mm, "end": v(-342.61, -66.8) * mm, "construction": true});
            skLineSegment(sketch, "E237", {"start": v(-342.61, -82.8) * mm, "end": v(-342.61, -66.8) * mm, "construction": true});
            skLineSegment(sketch, "E238.left", {"start": v(-485.24, 95.45) * mm, "end": v(-485.24, 91.96) * mm});
            skLineSegment(sketch, "E239", {"start": v(-483.65, 97.04) * mm, "end": v(-477.04, 97.04) * mm});
            skArc(sketch, "E240.filletArc", {"start": v(-483.65, 97.04) * mm, "mid": v(-484.77, 96.57) * mm, "end": v(-485.24, 95.45) * mm});
            skLineSegment(sketch, "E241", {"start": v(-473.87, 91.96) * mm, "end": v(-469.61, 91.96) * mm});
            skLineSegment(sketch, "E242.MirrorCS", {"start": v(-454, 95.45) * mm, "end": v(-454, 91.96) * mm});
            skLineSegment(sketch, "E243.MirrorCS", {"start": v(-455.58, 97.04) * mm, "end": v(-462.19, 97.04) * mm});
            skArc(sketch, "E244.MirrorCS", {"start": v(-455.58, 97.04) * mm, "mid": v(-454.46, 96.57) * mm, "end": v(-454, 95.45) * mm});
            skArc(sketch, "E245", {"start": v(-475.46, 95.45) * mm, "mid": v(-475.92, 96.57) * mm, "end": v(-477.04, 97.04) * mm});
            skArc(sketch, "E246", {"start": v(-475.46, 93.55) * mm, "mid": v(-475, 92.42) * mm, "end": v(-473.87, 91.96) * mm});
            skArc(sketch, "E247", {"start": v(-465.36, 91.96) * mm, "mid": v(-464.24, 92.42) * mm, "end": v(-463.77, 93.55) * mm});
            skArc(sketch, "E248", {"start": v(-462.19, 97.04) * mm, "mid": v(-463.3, 96.57) * mm, "end": v(-463.77, 95.45) * mm});
            skLineSegment(sketch, "E249", {"start": v(-465.36, 91.96) * mm, "end": v(-469.61, 91.96) * mm});
            skArc(sketch, "E250", {"start": v(-488.41, 91.96) * mm, "mid": v(-486.82, 90.37) * mm, "end": v(-485.24, 91.96) * mm});
            skArc(sketch, "E251", {"start": v(-454, 91.96) * mm, "mid": v(-452.4, 90.37) * mm, "end": v(-450.82, 91.96) * mm});
            skLineSegment(sketch, "E252.0", {"start": v(-485.24, 91.96) * mm, "end": v(-454, 91.96) * mm, "construction": true});
            skLineSegment(sketch, "E253.0", {"start": v(-477.04, 95.45) * mm, "end": v(-462.19, 95.45) * mm, "construction": true});
            skLineSegment(sketch, "E254.0", {"start": v(-483.65, 97.04) * mm, "end": v(-455.58, 97.04) * mm, "construction": true});
            skLineSegment(sketch, "E255", {"start": v(-483.65, 97.04) * mm, "end": v(-483.65, 91.96) * mm, "construction": true});
            skLineSegment(sketch, "E256", {"start": v(-475.46, 95.45) * mm, "end": v(-475.46, 93.55) * mm});
            skLineSegment(sketch, "E257", {"start": v(-463.77, 95.45) * mm, "end": v(-463.77, 93.55) * mm});
            skLineSegment(sketch, "E258.trimOffspring", {"start": v(-450.82, 91.96) * mm, "end": v(-342.61, 91.96) * mm});
            skLineSegment(sketch, "E259.MirrorCS", {"start": v(-593.38, 76.21) * mm, "end": v(-596.61, 76.21) * mm});
            skLineSegment(sketch, "E260", {"start": v(-593.38, 44.2) * mm, "end": v(-596.61, 44.2) * mm});
            skArc(sketch, "E261", {"start": v(-592.58, 73.25) * mm, "mid": v(-591.84, 75.04) * mm, "end": v(-593.38, 76.21) * mm});
            skArc(sketch, "E262", {"start": v(-592.58, 73.25) * mm, "mid": v(-593.16, 72.67) * mm, "end": v(-593.38, 71.87) * mm});
            skArc(sketch, "E263.MirrorCS", {"start": v(-592.58, 47.17) * mm, "mid": v(-591.84, 45.38) * mm, "end": v(-593.38, 44.2) * mm});
            skArc(sketch, "E264.MirrorCS", {"start": v(-592.58, 47.17) * mm, "mid": v(-593.16, 47.75) * mm, "end": v(-593.38, 48.55) * mm});
            skLineSegment(sketch, "E265.trimOffspring", {"start": v(-593.38, 48.55) * mm, "end": v(-593.38, 71.87) * mm});
            skLineSegment(sketch, "E266", {"start": v(-593.38, 76.21) * mm, "end": v(-593.38, 71.87) * mm, "construction": true});
            skLineSegment(sketch, "E267", {"start": v(-593.38, 48.55) * mm, "end": v(-593.38, 44.2) * mm, "construction": true});
            skLineSegment(sketch, "E268", {"start": v(-593.38, 60.2) * mm, "end": v(-596.61, 60.2) * mm, "construction": true});
            skLineSegment(sketch, "E269", {"start": v(-596.61, 76.21) * mm, "end": v(-596.61, 60.2) * mm, "construction": true});
            skLineSegment(sketch, "E270.MirrorCS", {"start": v(-593.38, -50.79) * mm, "end": v(-596.61, -50.79) * mm});
            skLineSegment(sketch, "E271", {"start": v(-593.38, -82.8) * mm, "end": v(-596.61, -82.8) * mm});
            skArc(sketch, "E272", {"start": v(-592.58, -53.75) * mm, "mid": v(-591.84, -51.96) * mm, "end": v(-593.38, -50.79) * mm});
            skArc(sketch, "E273", {"start": v(-592.58, -53.75) * mm, "mid": v(-593.16, -54.33) * mm, "end": v(-593.38, -55.13) * mm});
            skArc(sketch, "E274.MirrorCS", {"start": v(-592.58, -79.83) * mm, "mid": v(-591.84, -81.62) * mm, "end": v(-593.38, -82.8) * mm});
            skArc(sketch, "E275.MirrorCS", {"start": v(-592.58, -79.83) * mm, "mid": v(-593.16, -79.25) * mm, "end": v(-593.38, -78.45) * mm});
            skLineSegment(sketch, "E276.trimOffspring", {"start": v(-593.38, -78.45) * mm, "end": v(-593.38, -55.13) * mm});
            skLineSegment(sketch, "E277", {"start": v(-593.38, -50.79) * mm, "end": v(-593.38, -55.13) * mm, "construction": true});
            skLineSegment(sketch, "E278", {"start": v(-593.38, -78.45) * mm, "end": v(-593.38, -82.8) * mm, "construction": true});
            skLineSegment(sketch, "E279", {"start": v(-593.38, -66.8) * mm, "end": v(-596.61, -66.8) * mm, "construction": true});
            skLineSegment(sketch, "E280", {"start": v(-596.61, -50.79) * mm, "end": v(-596.61, -66.8) * mm, "construction": true});
            skLineSegment(sketch, "E281.bottom", {"start": v(-855.04, 925.97) * mm, "end": v(-753.19, 925.97) * mm});
            skLineSegment(sketch, "E281.top", {"start": v(-855.04, 729.12) * mm, "end": v(-610.63, 729.12) * mm});
            skLineSegment(sketch, "E281.left", {"start": v(-855.04, 925.97) * mm, "end": v(-855.04, 913.02) * mm});
            skLineSegment(sketch, "E281.right", {"start": v(-607.39, 925.97) * mm, "end": v(-607.39, 827.8) * mm});
            skArc(sketch, "E282", {"start": v(-747.43, 736.4) * mm, "mid": v(-749.21, 737.13) * mm, "end": v(-750.4, 735.6) * mm});
            skArc(sketch, "E283", {"start": v(-747.43, 736.4) * mm, "mid": v(-746.85, 735.81) * mm, "end": v(-746.05, 735.6) * mm});
            skArc(sketch, "E284.MirrorCS", {"start": v(-721.35, 736.4) * mm, "mid": v(-719.56, 737.13) * mm, "end": v(-718.39, 735.6) * mm});
            skArc(sketch, "E285.MirrorCS", {"start": v(-721.35, 736.4) * mm, "mid": v(-721.93, 735.81) * mm, "end": v(-722.72, 735.6) * mm});
            skLineSegment(sketch, "E286.trimOffspring", {"start": v(-722.72, 735.6) * mm, "end": v(-746.05, 735.6) * mm});
            skLineSegment(sketch, "E287", {"start": v(-750.4, 735.6) * mm, "end": v(-746.05, 735.6) * mm, "construction": true});
            skLineSegment(sketch, "E288", {"start": v(-722.72, 735.6) * mm, "end": v(-718.39, 735.6) * mm, "construction": true});
            skLineSegment(sketch, "E289", {"start": v(-734.39, 735.6) * mm, "end": v(-734.39, 729.12) * mm, "construction": true});
            skLineSegment(sketch, "E290", {"start": v(-750.4, 729.12) * mm, "end": v(-734.39, 729.12) * mm, "construction": true});
            skLineSegment(sketch, "E291.left", {"start": v(-858.53, 878.6) * mm, "end": v(-855.04, 878.6) * mm});
            skLineSegment(sketch, "E292", {"start": v(-860.12, 880.19) * mm, "end": v(-860.12, 886.8) * mm});
            skArc(sketch, "E293.filletArc", {"start": v(-860.12, 880.19) * mm, "mid": v(-859.65, 879.06) * mm, "end": v(-858.53, 878.6) * mm});
            skLineSegment(sketch, "E294", {"start": v(-855.04, 889.97) * mm, "end": v(-855.04, 894.22) * mm});
            skLineSegment(sketch, "E295.MirrorCS", {"start": v(-858.53, 909.84) * mm, "end": v(-855.04, 909.84) * mm});
            skLineSegment(sketch, "E296.MirrorCS", {"start": v(-860.12, 908.25) * mm, "end": v(-860.12, 901.65) * mm});
            skArc(sketch, "E297.MirrorCS", {"start": v(-860.12, 908.25) * mm, "mid": v(-859.65, 909.38) * mm, "end": v(-858.53, 909.84) * mm});
            skArc(sketch, "E298", {"start": v(-858.53, 888.38) * mm, "mid": v(-859.65, 887.91) * mm, "end": v(-860.12, 886.8) * mm});
            skArc(sketch, "E299", {"start": v(-856.63, 888.38) * mm, "mid": v(-855.5, 888.84) * mm, "end": v(-855.04, 889.97) * mm});
            skArc(sketch, "E300", {"start": v(-855.04, 898.48) * mm, "mid": v(-855.5, 899.6) * mm, "end": v(-856.63, 900.06) * mm});
            skArc(sketch, "E301", {"start": v(-860.12, 901.65) * mm, "mid": v(-859.65, 900.53) * mm, "end": v(-858.53, 900.06) * mm});
            skLineSegment(sketch, "E302", {"start": v(-855.04, 898.48) * mm, "end": v(-855.04, 894.22) * mm});
            skArc(sketch, "E303", {"start": v(-855.04, 875.42) * mm, "mid": v(-853.45, 877.01) * mm, "end": v(-855.04, 878.6) * mm});
            skArc(sketch, "E304", {"start": v(-855.04, 909.84) * mm, "mid": v(-853.45, 911.43) * mm, "end": v(-855.04, 913.02) * mm});
            skLineSegment(sketch, "E305.0", {"start": v(-858.53, 886.8) * mm, "end": v(-858.53, 901.65) * mm, "construction": true});
            skLineSegment(sketch, "E306.0", {"start": v(-860.12, 880.19) * mm, "end": v(-860.12, 908.25) * mm, "construction": true});
            skLineSegment(sketch, "E307", {"start": v(-855.04, 880.19) * mm, "end": v(-860.12, 880.19) * mm, "construction": true});
            skLineSegment(sketch, "E308", {"start": v(-858.53, 888.38) * mm, "end": v(-856.63, 888.38) * mm});
            skLineSegment(sketch, "E309", {"start": v(-858.53, 900.06) * mm, "end": v(-856.63, 900.06) * mm});
            skLineSegment(sketch, "E310.left", {"start": v(-858.53, 751.6) * mm, "end": v(-855.04, 751.6) * mm});
            skLineSegment(sketch, "E311", {"start": v(-860.12, 753.19) * mm, "end": v(-860.12, 759.8) * mm});
            skArc(sketch, "E312.filletArc", {"start": v(-860.12, 753.19) * mm, "mid": v(-859.65, 752.06) * mm, "end": v(-858.53, 751.6) * mm});
            skLineSegment(sketch, "E313", {"start": v(-855.04, 762.97) * mm, "end": v(-855.04, 767.22) * mm});
            skLineSegment(sketch, "E314.MirrorCS", {"start": v(-858.53, 782.84) * mm, "end": v(-855.04, 782.84) * mm});
            skLineSegment(sketch, "E315.MirrorCS", {"start": v(-860.12, 781.25) * mm, "end": v(-860.12, 774.65) * mm});
            skArc(sketch, "E316.MirrorCS", {"start": v(-860.12, 781.25) * mm, "mid": v(-859.65, 782.38) * mm, "end": v(-858.53, 782.84) * mm});
            skArc(sketch, "E317", {"start": v(-858.53, 761.38) * mm, "mid": v(-859.65, 760.91) * mm, "end": v(-860.12, 759.8) * mm});
            skArc(sketch, "E318", {"start": v(-856.63, 761.38) * mm, "mid": v(-855.5, 761.84) * mm, "end": v(-855.04, 762.97) * mm});
            skArc(sketch, "E319", {"start": v(-855.04, 771.48) * mm, "mid": v(-855.5, 772.6) * mm, "end": v(-856.63, 773.06) * mm});
            skArc(sketch, "E320", {"start": v(-860.12, 774.65) * mm, "mid": v(-859.65, 773.53) * mm, "end": v(-858.53, 773.06) * mm});
            skLineSegment(sketch, "E321", {"start": v(-855.04, 771.48) * mm, "end": v(-855.04, 767.22) * mm});
            skArc(sketch, "E322", {"start": v(-855.04, 748.42) * mm, "mid": v(-853.45, 750.01) * mm, "end": v(-855.04, 751.6) * mm});
            skArc(sketch, "E323", {"start": v(-855.04, 782.84) * mm, "mid": v(-853.45, 784.43) * mm, "end": v(-855.04, 786.02) * mm});
            skLineSegment(sketch, "E324.0", {"start": v(-858.53, 759.8) * mm, "end": v(-858.53, 774.65) * mm, "construction": true});
            skLineSegment(sketch, "E325.0", {"start": v(-860.12, 753.19) * mm, "end": v(-860.12, 781.25) * mm, "construction": true});
            skLineSegment(sketch, "E326", {"start": v(-860.12, 753.19) * mm, "end": v(-855.04, 753.08) * mm, "construction": true});
            skLineSegment(sketch, "E327", {"start": v(-858.53, 761.38) * mm, "end": v(-856.63, 761.38) * mm});
            skLineSegment(sketch, "E328", {"start": v(-858.53, 773.06) * mm, "end": v(-856.63, 773.06) * mm});
            skLineSegment(sketch, "E329.trimOffspring", {"start": v(-855.04, 748.42) * mm, "end": v(-855.04, 729.12) * mm});
            skLineSegment(sketch, "E330.trimOffspring", {"start": v(-855.04, 875.42) * mm, "end": v(-855.04, 786.02) * mm});
            skLineSegment(sketch, "E331.left", {"start": v(-750.01, 929.46) * mm, "end": v(-750.01, 925.97) * mm});
            skLineSegment(sketch, "E332", {"start": v(-748.42, 931.05) * mm, "end": v(-741.82, 931.05) * mm});
            skArc(sketch, "E333.filletArc", {"start": v(-748.42, 931.05) * mm, "mid": v(-749.55, 930.59) * mm, "end": v(-750.01, 929.46) * mm});
            skLineSegment(sketch, "E334", {"start": v(-738.64, 925.97) * mm, "end": v(-734.39, 925.97) * mm});
            skLineSegment(sketch, "E335.MirrorCS", {"start": v(-718.77, 929.46) * mm, "end": v(-718.77, 925.97) * mm});
            skLineSegment(sketch, "E336.MirrorCS", {"start": v(-720.36, 931.05) * mm, "end": v(-726.96, 931.05) * mm});
            skArc(sketch, "E337.MirrorCS", {"start": v(-720.36, 931.05) * mm, "mid": v(-719.23, 930.59) * mm, "end": v(-718.77, 929.46) * mm});
            skArc(sketch, "E338", {"start": v(-740.23, 929.46) * mm, "mid": v(-740.7, 930.59) * mm, "end": v(-741.82, 931.05) * mm});
            skArc(sketch, "E339", {"start": v(-740.23, 927.56) * mm, "mid": v(-739.77, 926.44) * mm, "end": v(-738.64, 925.97) * mm});
            skArc(sketch, "E340", {"start": v(-730.13, 925.97) * mm, "mid": v(-729.01, 926.44) * mm, "end": v(-728.55, 927.56) * mm});
            skArc(sketch, "E341", {"start": v(-726.96, 931.05) * mm, "mid": v(-728.08, 930.59) * mm, "end": v(-728.55, 929.46) * mm});
            skLineSegment(sketch, "E342", {"start": v(-730.13, 925.97) * mm, "end": v(-734.39, 925.97) * mm});
            skArc(sketch, "E343", {"start": v(-753.19, 925.97) * mm, "mid": v(-751.6, 924.38) * mm, "end": v(-750.01, 925.97) * mm});
            skArc(sketch, "E344", {"start": v(-718.77, 925.97) * mm, "mid": v(-717.18, 924.38) * mm, "end": v(-715.6, 925.97) * mm});
            skLineSegment(sketch, "E345.0", {"start": v(-750.01, 925.97) * mm, "end": v(-718.77, 925.97) * mm, "construction": true});
            skLineSegment(sketch, "E346.0", {"start": v(-741.82, 929.46) * mm, "end": v(-726.96, 929.46) * mm, "construction": true});
            skLineSegment(sketch, "E347.0", {"start": v(-748.42, 931.05) * mm, "end": v(-720.36, 931.05) * mm, "construction": true});
            skLineSegment(sketch, "E348", {"start": v(-748.42, 931.05) * mm, "end": v(-748.42, 925.97) * mm, "construction": true});
            skLineSegment(sketch, "E349", {"start": v(-740.23, 929.46) * mm, "end": v(-740.23, 927.56) * mm});
            skLineSegment(sketch, "E350", {"start": v(-728.55, 929.46) * mm, "end": v(-728.55, 927.56) * mm});
            skLineSegment(sketch, "E351.trimOffspring", {"start": v(-715.6, 925.97) * mm, "end": v(-607.39, 925.97) * mm});
            skLineSegment(sketch, "E352.bottom", {"start": v(-1417.07, 893.34) * mm, "end": v(-1308.87, 893.34) * mm});
            skLineSegment(sketch, "E352.top", {"start": v(-1413.83, 696.49) * mm, "end": v(-1166.3, 696.49) * mm});
            skLineSegment(sketch, "E352.left", {"start": v(-1417.07, 893.34) * mm, "end": v(-1417.07, 795.17) * mm});
            skLineSegment(sketch, "E352.right", {"start": v(-1163.07, 893.34) * mm, "end": v(-1163.07, 795.17) * mm});
            skLineSegment(sketch, "E353.left", {"start": v(-1305.7, 896.83) * mm, "end": v(-1305.7, 893.34) * mm});
            skLineSegment(sketch, "E354", {"start": v(-1304.1, 898.42) * mm, "end": v(-1297.5, 898.42) * mm});
            skArc(sketch, "E355.filletArc", {"start": v(-1304.1, 898.42) * mm, "mid": v(-1305.23, 897.95) * mm, "end": v(-1305.7, 896.83) * mm});
            skLineSegment(sketch, "E356", {"start": v(-1294.32, 893.34) * mm, "end": v(-1290.07, 893.34) * mm});
            skLineSegment(sketch, "E357.MirrorCS", {"start": v(-1274.45, 896.83) * mm, "end": v(-1274.45, 893.34) * mm});
            skLineSegment(sketch, "E358.MirrorCS", {"start": v(-1276.04, 898.42) * mm, "end": v(-1282.64, 898.42) * mm});
            skArc(sketch, "E359.MirrorCS", {"start": v(-1276.04, 898.42) * mm, "mid": v(-1274.91, 897.95) * mm, "end": v(-1274.45, 896.83) * mm});
            skArc(sketch, "E360", {"start": v(-1295.91, 896.83) * mm, "mid": v(-1296.38, 897.95) * mm, "end": v(-1297.5, 898.42) * mm});
            skArc(sketch, "E361", {"start": v(-1295.91, 894.93) * mm, "mid": v(-1295.45, 893.8) * mm, "end": v(-1294.32, 893.34) * mm});
            skArc(sketch, "E362", {"start": v(-1285.82, 893.34) * mm, "mid": v(-1284.7, 893.8) * mm, "end": v(-1284.23, 894.93) * mm});
            skArc(sketch, "E363", {"start": v(-1282.64, 898.42) * mm, "mid": v(-1283.76, 897.95) * mm, "end": v(-1284.23, 896.83) * mm});
            skLineSegment(sketch, "E364", {"start": v(-1285.82, 893.34) * mm, "end": v(-1290.07, 893.34) * mm});
            skArc(sketch, "E365", {"start": v(-1308.87, 893.34) * mm, "mid": v(-1307.28, 891.75) * mm, "end": v(-1305.7, 893.34) * mm});
            skArc(sketch, "E366", {"start": v(-1274.45, 893.34) * mm, "mid": v(-1272.86, 891.75) * mm, "end": v(-1271.27, 893.34) * mm});
            skLineSegment(sketch, "E367.0", {"start": v(-1305.7, 893.34) * mm, "end": v(-1274.45, 893.34) * mm, "construction": true});
            skLineSegment(sketch, "E368.0", {"start": v(-1297.5, 896.83) * mm, "end": v(-1282.64, 896.83) * mm, "construction": true});
            skLineSegment(sketch, "E369.0", {"start": v(-1304.1, 898.42) * mm, "end": v(-1276.04, 898.42) * mm, "construction": true});
            skLineSegment(sketch, "E370", {"start": v(-1304.1, 898.42) * mm, "end": v(-1304.1, 893.34) * mm, "construction": true});
            skLineSegment(sketch, "E371", {"start": v(-1295.91, 896.83) * mm, "end": v(-1295.91, 894.93) * mm});
            skLineSegment(sketch, "E372", {"start": v(-1284.23, 896.83) * mm, "end": v(-1284.23, 894.93) * mm});
            skLineSegment(sketch, "E373.trimOffspring", {"start": v(-1271.27, 893.34) * mm, "end": v(-1163.07, 893.34) * mm});
            skLineSegment(sketch, "E374.bottom", {"start": v(-821.7, 887.87) * mm, "end": v(-647.08, 887.87) * mm});
            skLineSegment(sketch, "E374.top", {"start": v(-821.7, 767.22) * mm, "end": v(-647.08, 767.22) * mm});
            skLineSegment(sketch, "E374.left", {"start": v(-823.29, 886.28) * mm, "end": v(-823.29, 768.8) * mm});
            skLineSegment(sketch, "E374.right", {"start": v(-645.49, 886.28) * mm, "end": v(-645.49, 768.8) * mm});
            skLineSegment(sketch, "E375", {"start": v(-750.4, 735.6) * mm, "end": v(-750.4, 729.12) * mm});
            skLineSegment(sketch, "E376", {"start": v(-718.39, 735.6) * mm, "end": v(-718.39, 729.12) * mm});
            skPoint(sketch, "E377.visualSharp", {"position": v(-823.29, 887.87) * mm});
            skArc(sketch, "E377.filletArc", {"start": v(-821.7, 887.87) * mm, "mid": v(-822.82, 887.4) * mm, "end": v(-823.29, 886.28) * mm});
            skPoint(sketch, "E378.visualSharp", {"position": v(-645.49, 887.87) * mm});
            skArc(sketch, "E378.filletArc", {"start": v(-645.49, 886.28) * mm, "mid": v(-645.95, 887.4) * mm, "end": v(-647.08, 887.87) * mm});
            skPoint(sketch, "E379.visualSharp", {"position": v(-645.49, 767.22) * mm});
            skArc(sketch, "E379.filletArc", {"start": v(-647.08, 767.22) * mm, "mid": v(-645.95, 767.69) * mm, "end": v(-645.49, 768.8) * mm});
            skPoint(sketch, "E380.visualSharp", {"position": v(-823.29, 767.22) * mm});
            skArc(sketch, "E380.filletArc", {"start": v(-823.29, 768.8) * mm, "mid": v(-822.82, 767.69) * mm, "end": v(-821.7, 767.22) * mm});
            skLineSegment(sketch, "E381.bottom", {"start": v(-1377.38, 855.24) * mm, "end": v(-1202.76, 855.24) * mm});
            skLineSegment(sketch, "E381.top", {"start": v(-1377.38, 734.59) * mm, "end": v(-1202.76, 734.59) * mm});
            skLineSegment(sketch, "E381.left", {"start": v(-1378.97, 853.65) * mm, "end": v(-1378.97, 736.18) * mm});
            skLineSegment(sketch, "E381.right", {"start": v(-1201.17, 853.65) * mm, "end": v(-1201.17, 736.18) * mm});
            skPoint(sketch, "E382.visualSharp", {"position": v(-1378.97, 855.24) * mm});
            skArc(sketch, "E382.filletArc", {"start": v(-1377.38, 855.24) * mm, "mid": v(-1378.5, 854.77) * mm, "end": v(-1378.97, 853.65) * mm});
            skPoint(sketch, "E383.visualSharp", {"position": v(-1201.17, 855.24) * mm});
            skArc(sketch, "E383.filletArc", {"start": v(-1201.17, 853.65) * mm, "mid": v(-1201.64, 854.77) * mm, "end": v(-1202.76, 855.24) * mm});
            skPoint(sketch, "E384.visualSharp", {"position": v(-1201.17, 734.59) * mm});
            skArc(sketch, "E384.filletArc", {"start": v(-1202.76, 734.59) * mm, "mid": v(-1201.64, 735.05) * mm, "end": v(-1201.17, 736.18) * mm});
            skPoint(sketch, "E385.visualSharp", {"position": v(-1378.97, 734.59) * mm});
            skArc(sketch, "E385.filletArc", {"start": v(-1378.97, 736.18) * mm, "mid": v(-1378.5, 735.05) * mm, "end": v(-1377.38, 734.59) * mm});
            skPoint(sketch, "E386.orphan", {"position": v(-823.29, 827.55) * mm});
            skPoint(sketch, "E387.orphan", {"position": v(-734.39, 767.22) * mm});
            skLineSegment(sketch, "E388.bottom", {"start": v(-1520.97, 469.45) * mm, "end": v(-1419.11, 469.45) * mm});
            skLineSegment(sketch, "E388.top", {"start": v(-1520.97, 272.6) * mm, "end": v(-1273.32, 272.6) * mm});
            skLineSegment(sketch, "E388.left", {"start": v(-1520.97, 469.45) * mm, "end": v(-1520.97, 456.5) * mm});
            skLineSegment(sketch, "E388.right", {"start": v(-1273.32, 370.77) * mm, "end": v(-1273.32, 272.6) * mm});
            skArc(sketch, "E389", {"start": v(-1413.36, 279.87) * mm, "mid": v(-1415.14, 280.6) * mm, "end": v(-1416.32, 279.07) * mm});
            skArc(sketch, "E390", {"start": v(-1413.36, 279.87) * mm, "mid": v(-1412.78, 279.29) * mm, "end": v(-1411.98, 279.07) * mm});
            skArc(sketch, "E391.MirrorCS", {"start": v(-1387.28, 279.87) * mm, "mid": v(-1385.5, 280.6) * mm, "end": v(-1384.31, 279.07) * mm});
            skArc(sketch, "E392.MirrorCS", {"start": v(-1387.28, 279.87) * mm, "mid": v(-1387.86, 279.29) * mm, "end": v(-1388.65, 279.07) * mm});
            skLineSegment(sketch, "E393.trimOffspring", {"start": v(-1388.65, 279.07) * mm, "end": v(-1411.98, 279.07) * mm});
            skLineSegment(sketch, "E394", {"start": v(-1416.32, 279.07) * mm, "end": v(-1411.98, 279.07) * mm, "construction": true});
            skLineSegment(sketch, "E395", {"start": v(-1388.65, 279.07) * mm, "end": v(-1384.31, 279.07) * mm, "construction": true});
            skLineSegment(sketch, "E396", {"start": v(-1400.32, 279.07) * mm, "end": v(-1400.32, 272.6) * mm, "construction": true});
            skLineSegment(sketch, "E397", {"start": v(-1416.32, 272.6) * mm, "end": v(-1400.32, 272.6) * mm, "construction": true});
            skLineSegment(sketch, "E398.left", {"start": v(-1524.46, 422.08) * mm, "end": v(-1520.97, 422.08) * mm});
            skLineSegment(sketch, "E399", {"start": v(-1526.05, 423.66) * mm, "end": v(-1526.05, 430.27) * mm});
            skArc(sketch, "E400.filletArc", {"start": v(-1526.05, 423.66) * mm, "mid": v(-1525.58, 422.54) * mm, "end": v(-1524.46, 422.08) * mm});
            skLineSegment(sketch, "E401", {"start": v(-1520.97, 433.44) * mm, "end": v(-1520.97, 437.7) * mm});
            skLineSegment(sketch, "E402.MirrorCS", {"start": v(-1524.46, 453.32) * mm, "end": v(-1520.97, 453.32) * mm});
            skLineSegment(sketch, "E403.MirrorCS", {"start": v(-1526.05, 451.73) * mm, "end": v(-1526.05, 445.13) * mm});
            skArc(sketch, "E404.MirrorCS", {"start": v(-1526.05, 451.73) * mm, "mid": v(-1525.58, 452.85) * mm, "end": v(-1524.46, 453.32) * mm});
            skArc(sketch, "E405", {"start": v(-1524.46, 431.85) * mm, "mid": v(-1525.58, 431.39) * mm, "end": v(-1526.05, 430.27) * mm});
            skArc(sketch, "E406", {"start": v(-1522.55, 431.85) * mm, "mid": v(-1521.43, 432.32) * mm, "end": v(-1520.97, 433.44) * mm});
            skArc(sketch, "E407", {"start": v(-1520.97, 441.95) * mm, "mid": v(-1521.43, 443.07) * mm, "end": v(-1522.55, 443.54) * mm});
            skArc(sketch, "E408", {"start": v(-1526.05, 445.13) * mm, "mid": v(-1525.58, 444) * mm, "end": v(-1524.46, 443.54) * mm});
            skLineSegment(sketch, "E409", {"start": v(-1520.97, 441.95) * mm, "end": v(-1520.97, 437.7) * mm});
            skArc(sketch, "E410", {"start": v(-1520.97, 418.9) * mm, "mid": v(-1519.38, 420.49) * mm, "end": v(-1520.97, 422.08) * mm});
            skArc(sketch, "E411", {"start": v(-1520.97, 453.32) * mm, "mid": v(-1519.38, 454.9) * mm, "end": v(-1520.97, 456.5) * mm});
            skLineSegment(sketch, "E412.0", {"start": v(-1524.46, 430.27) * mm, "end": v(-1524.46, 445.13) * mm, "construction": true});
            skLineSegment(sketch, "E413.0", {"start": v(-1526.05, 423.66) * mm, "end": v(-1526.05, 451.73) * mm, "construction": true});
            skLineSegment(sketch, "E414", {"start": v(-1520.97, 423.66) * mm, "end": v(-1526.05, 423.66) * mm, "construction": true});
            skLineSegment(sketch, "E415", {"start": v(-1524.46, 431.85) * mm, "end": v(-1522.55, 431.85) * mm});
            skLineSegment(sketch, "E416", {"start": v(-1524.46, 443.54) * mm, "end": v(-1522.55, 443.54) * mm});
            skLineSegment(sketch, "E417.left", {"start": v(-1524.46, 295.08) * mm, "end": v(-1520.97, 295.08) * mm});
            skLineSegment(sketch, "E418", {"start": v(-1526.05, 296.66) * mm, "end": v(-1526.05, 303.27) * mm});
            skArc(sketch, "E419.filletArc", {"start": v(-1526.05, 296.66) * mm, "mid": v(-1525.58, 295.54) * mm, "end": v(-1524.46, 295.08) * mm});
            skLineSegment(sketch, "E420", {"start": v(-1520.97, 306.44) * mm, "end": v(-1520.97, 310.7) * mm});
            skLineSegment(sketch, "E421.MirrorCS", {"start": v(-1524.46, 326.32) * mm, "end": v(-1520.97, 326.32) * mm});
            skLineSegment(sketch, "E422.MirrorCS", {"start": v(-1526.05, 324.73) * mm, "end": v(-1526.05, 318.13) * mm});
            skArc(sketch, "E423.MirrorCS", {"start": v(-1526.05, 324.73) * mm, "mid": v(-1525.58, 325.85) * mm, "end": v(-1524.46, 326.32) * mm});
            skArc(sketch, "E424", {"start": v(-1524.46, 304.85) * mm, "mid": v(-1525.58, 304.4) * mm, "end": v(-1526.05, 303.27) * mm});
            skArc(sketch, "E425", {"start": v(-1522.55, 304.85) * mm, "mid": v(-1521.43, 305.32) * mm, "end": v(-1520.97, 306.44) * mm});
            skArc(sketch, "E426", {"start": v(-1520.97, 314.95) * mm, "mid": v(-1521.43, 316.07) * mm, "end": v(-1522.55, 316.54) * mm});
            skArc(sketch, "E427", {"start": v(-1526.05, 318.13) * mm, "mid": v(-1525.58, 317) * mm, "end": v(-1524.46, 316.54) * mm});
            skLineSegment(sketch, "E428", {"start": v(-1520.97, 314.95) * mm, "end": v(-1520.97, 310.7) * mm});
            skArc(sketch, "E429", {"start": v(-1520.97, 291.9) * mm, "mid": v(-1519.38, 293.49) * mm, "end": v(-1520.97, 295.08) * mm});
            skArc(sketch, "E430", {"start": v(-1520.97, 326.32) * mm, "mid": v(-1519.38, 327.9) * mm, "end": v(-1520.97, 329.5) * mm});
            skLineSegment(sketch, "E431.0", {"start": v(-1524.46, 303.27) * mm, "end": v(-1524.46, 318.13) * mm, "construction": true});
            skLineSegment(sketch, "E432.0", {"start": v(-1526.05, 296.66) * mm, "end": v(-1526.05, 324.73) * mm, "construction": true});
            skLineSegment(sketch, "E433", {"start": v(-1526.05, 296.66) * mm, "end": v(-1520.97, 296.55) * mm, "construction": true});
            skLineSegment(sketch, "E434", {"start": v(-1524.46, 304.85) * mm, "end": v(-1522.55, 304.85) * mm});
            skLineSegment(sketch, "E435", {"start": v(-1524.46, 316.54) * mm, "end": v(-1522.55, 316.54) * mm});
            skLineSegment(sketch, "E436.trimOffspring", {"start": v(-1520.97, 291.9) * mm, "end": v(-1520.97, 272.6) * mm});
            skLineSegment(sketch, "E437.trimOffspring", {"start": v(-1520.97, 418.9) * mm, "end": v(-1520.97, 329.5) * mm});
            skLineSegment(sketch, "E438.left", {"start": v(-1415.94, 472.94) * mm, "end": v(-1415.94, 469.45) * mm});
            skLineSegment(sketch, "E439", {"start": v(-1414.35, 474.53) * mm, "end": v(-1407.75, 474.53) * mm});
            skArc(sketch, "E440.filletArc", {"start": v(-1414.35, 474.53) * mm, "mid": v(-1415.47, 474.06) * mm, "end": v(-1415.94, 472.94) * mm});
            skLineSegment(sketch, "E441", {"start": v(-1404.57, 469.45) * mm, "end": v(-1400.32, 469.45) * mm});
            skLineSegment(sketch, "E442.MirrorCS", {"start": v(-1384.7, 472.94) * mm, "end": v(-1384.7, 469.45) * mm});
            skLineSegment(sketch, "E443.MirrorCS", {"start": v(-1386.28, 474.53) * mm, "end": v(-1392.89, 474.53) * mm});
            skArc(sketch, "E444.MirrorCS", {"start": v(-1386.28, 474.53) * mm, "mid": v(-1385.16, 474.06) * mm, "end": v(-1384.7, 472.94) * mm});
            skArc(sketch, "E445", {"start": v(-1406.16, 472.94) * mm, "mid": v(-1406.62, 474.06) * mm, "end": v(-1407.75, 474.53) * mm});
            skArc(sketch, "E446", {"start": v(-1406.16, 471.03) * mm, "mid": v(-1405.7, 469.91) * mm, "end": v(-1404.57, 469.45) * mm});
            skArc(sketch, "E447", {"start": v(-1396.06, 469.45) * mm, "mid": v(-1394.94, 469.91) * mm, "end": v(-1394.47, 471.03) * mm});
            skArc(sketch, "E448", {"start": v(-1392.89, 474.53) * mm, "mid": v(-1394, 474.06) * mm, "end": v(-1394.47, 472.94) * mm});
            skLineSegment(sketch, "E449", {"start": v(-1396.06, 469.45) * mm, "end": v(-1400.32, 469.45) * mm});
            skArc(sketch, "E450", {"start": v(-1419.11, 469.45) * mm, "mid": v(-1417.53, 467.86) * mm, "end": v(-1415.94, 469.45) * mm});
            skArc(sketch, "E451", {"start": v(-1384.7, 469.45) * mm, "mid": v(-1383.1, 467.86) * mm, "end": v(-1381.52, 469.45) * mm});
            skLineSegment(sketch, "E452.0", {"start": v(-1415.94, 469.45) * mm, "end": v(-1384.7, 469.45) * mm, "construction": true});
            skLineSegment(sketch, "E453.0", {"start": v(-1407.75, 472.94) * mm, "end": v(-1392.89, 472.94) * mm, "construction": true});
            skLineSegment(sketch, "E454.0", {"start": v(-1414.35, 474.53) * mm, "end": v(-1386.28, 474.53) * mm, "construction": true});
            skLineSegment(sketch, "E455", {"start": v(-1414.35, 474.53) * mm, "end": v(-1414.35, 469.45) * mm, "construction": true});
            skLineSegment(sketch, "E456", {"start": v(-1406.16, 472.94) * mm, "end": v(-1406.16, 471.03) * mm});
            skLineSegment(sketch, "E457", {"start": v(-1394.47, 472.94) * mm, "end": v(-1394.47, 471.03) * mm});
            skLineSegment(sketch, "E458.trimOffspring", {"start": v(-1381.52, 469.45) * mm, "end": v(-1276.56, 469.45) * mm});
            skLineSegment(sketch, "E459.bottom", {"start": v(-1968.01, 907.07) * mm, "end": v(-1863.05, 907.07) * mm});
            skLineSegment(sketch, "E459.top", {"start": v(-1971.25, 710.22) * mm, "end": v(-1717.25, 710.22) * mm});
            skLineSegment(sketch, "E459.left", {"start": v(-1971.25, 808.4) * mm, "end": v(-1971.25, 710.22) * mm});
            skLineSegment(sketch, "E459.right", {"start": v(-1717.25, 808.4) * mm, "end": v(-1717.25, 710.22) * mm});
            skLineSegment(sketch, "E460.left", {"start": v(-1859.87, 910.56) * mm, "end": v(-1859.87, 907.07) * mm});
            skLineSegment(sketch, "E461", {"start": v(-1858.29, 912.15) * mm, "end": v(-1851.68, 912.15) * mm});
            skArc(sketch, "E462.filletArc", {"start": v(-1858.29, 912.15) * mm, "mid": v(-1859.4, 911.68) * mm, "end": v(-1859.87, 910.56) * mm});
            skLineSegment(sketch, "E463", {"start": v(-1848.5, 907.07) * mm, "end": v(-1844.25, 907.07) * mm});
            skLineSegment(sketch, "E464.MirrorCS", {"start": v(-1828.63, 910.56) * mm, "end": v(-1828.63, 907.07) * mm});
            skLineSegment(sketch, "E465.MirrorCS", {"start": v(-1830.22, 912.15) * mm, "end": v(-1836.82, 912.15) * mm});
            skArc(sketch, "E466.MirrorCS", {"start": v(-1830.22, 912.15) * mm, "mid": v(-1829.1, 911.68) * mm, "end": v(-1828.63, 910.56) * mm});
            skArc(sketch, "E467", {"start": v(-1850.1, 910.56) * mm, "mid": v(-1850.56, 911.68) * mm, "end": v(-1851.68, 912.15) * mm});
            skArc(sketch, "E468", {"start": v(-1850.1, 908.66) * mm, "mid": v(-1849.63, 907.53) * mm, "end": v(-1848.5, 907.07) * mm});
            skArc(sketch, "E469", {"start": v(-1840, 907.07) * mm, "mid": v(-1838.88, 907.53) * mm, "end": v(-1838.41, 908.66) * mm});
            skArc(sketch, "E470", {"start": v(-1836.82, 912.15) * mm, "mid": v(-1837.95, 911.68) * mm, "end": v(-1838.41, 910.56) * mm});
            skLineSegment(sketch, "E471", {"start": v(-1840, 907.07) * mm, "end": v(-1844.25, 907.07) * mm});
            skArc(sketch, "E472", {"start": v(-1863.05, 907.07) * mm, "mid": v(-1861.46, 905.48) * mm, "end": v(-1859.87, 907.07) * mm});
            skArc(sketch, "E473", {"start": v(-1828.63, 907.07) * mm, "mid": v(-1827.04, 905.48) * mm, "end": v(-1825.46, 907.07) * mm});
            skLineSegment(sketch, "E474.0", {"start": v(-1859.87, 907.07) * mm, "end": v(-1828.63, 907.07) * mm, "construction": true});
            skLineSegment(sketch, "E475.0", {"start": v(-1851.68, 910.56) * mm, "end": v(-1836.82, 910.56) * mm, "construction": true});
            skLineSegment(sketch, "E476.0", {"start": v(-1858.29, 912.15) * mm, "end": v(-1830.22, 912.15) * mm, "construction": true});
            skLineSegment(sketch, "E477", {"start": v(-1858.29, 912.15) * mm, "end": v(-1858.29, 907.07) * mm, "construction": true});
            skLineSegment(sketch, "E478", {"start": v(-1850.1, 910.56) * mm, "end": v(-1850.1, 908.66) * mm});
            skLineSegment(sketch, "E479", {"start": v(-1838.41, 910.56) * mm, "end": v(-1838.41, 908.66) * mm});
            skLineSegment(sketch, "E480.trimOffspring", {"start": v(-1825.46, 907.07) * mm, "end": v(-1720.5, 907.07) * mm});
            skLineSegment(sketch, "E481.bottom", {"start": v(-1487.63, 431.35) * mm, "end": v(-1313, 431.35) * mm});
            skLineSegment(sketch, "E481.top", {"start": v(-1487.63, 310.7) * mm, "end": v(-1313, 310.7) * mm});
            skLineSegment(sketch, "E481.left", {"start": v(-1489.22, 429.76) * mm, "end": v(-1489.22, 312.28) * mm});
            skLineSegment(sketch, "E481.right", {"start": v(-1311.42, 429.76) * mm, "end": v(-1311.42, 312.28) * mm});
            skLineSegment(sketch, "E482", {"start": v(-1416.32, 279.07) * mm, "end": v(-1416.32, 272.6) * mm});
            skLineSegment(sketch, "E483", {"start": v(-1384.31, 279.07) * mm, "end": v(-1384.31, 272.6) * mm});
            skPoint(sketch, "E484.visualSharp", {"position": v(-1489.22, 431.35) * mm});
            skArc(sketch, "E484.filletArc", {"start": v(-1487.63, 431.35) * mm, "mid": v(-1488.75, 430.88) * mm, "end": v(-1489.22, 429.76) * mm});
            skPoint(sketch, "E485.visualSharp", {"position": v(-1311.42, 431.35) * mm});
            skArc(sketch, "E485.filletArc", {"start": v(-1311.42, 429.76) * mm, "mid": v(-1311.88, 430.88) * mm, "end": v(-1313, 431.35) * mm});
            skPoint(sketch, "E486.visualSharp", {"position": v(-1311.42, 310.7) * mm});
            skArc(sketch, "E486.filletArc", {"start": v(-1313, 310.7) * mm, "mid": v(-1311.88, 311.16) * mm, "end": v(-1311.42, 312.28) * mm});
            skPoint(sketch, "E487.visualSharp", {"position": v(-1489.22, 310.7) * mm});
            skArc(sketch, "E487.filletArc", {"start": v(-1489.22, 312.28) * mm, "mid": v(-1488.75, 311.16) * mm, "end": v(-1487.63, 310.7) * mm});
            skLineSegment(sketch, "E488.bottom", {"start": v(-1931.56, 868.97) * mm, "end": v(-1756.94, 868.97) * mm});
            skLineSegment(sketch, "E488.top", {"start": v(-1931.56, 748.32) * mm, "end": v(-1756.94, 748.32) * mm});
            skLineSegment(sketch, "E488.left", {"start": v(-1933.15, 867.38) * mm, "end": v(-1933.15, 749.9) * mm});
            skLineSegment(sketch, "E488.right", {"start": v(-1755.35, 867.38) * mm, "end": v(-1755.35, 749.9) * mm});
            skPoint(sketch, "E489.visualSharp", {"position": v(-1933.15, 868.97) * mm});
            skArc(sketch, "E489.filletArc", {"start": v(-1931.56, 868.97) * mm, "mid": v(-1932.69, 868.5) * mm, "end": v(-1933.15, 867.38) * mm});
            skPoint(sketch, "E490.visualSharp", {"position": v(-1755.35, 868.97) * mm});
            skArc(sketch, "E490.filletArc", {"start": v(-1755.35, 867.38) * mm, "mid": v(-1755.82, 868.5) * mm, "end": v(-1756.94, 868.97) * mm});
            skPoint(sketch, "E491.visualSharp", {"position": v(-1755.35, 748.32) * mm});
            skArc(sketch, "E491.filletArc", {"start": v(-1756.94, 748.32) * mm, "mid": v(-1755.82, 748.78) * mm, "end": v(-1755.35, 749.9) * mm});
            skPoint(sketch, "E492.visualSharp", {"position": v(-1933.15, 748.32) * mm});
            skArc(sketch, "E492.filletArc", {"start": v(-1933.15, 749.9) * mm, "mid": v(-1932.69, 748.78) * mm, "end": v(-1931.56, 748.32) * mm});
            skPoint(sketch, "E493.orphan", {"position": v(-1933.15, 808.64) * mm});
            skPoint(sketch, "E494.orphan", {"position": v(-1844.25, 748.32) * mm});
            skPoint(sketch, "E495.orphan", {"position": v(-1489.22, 371.02) * mm});
            skPoint(sketch, "E496.orphan", {"position": v(-1400.32, 310.7) * mm});
            skLineSegment(sketch, "E497", {"start": v(-1035.27, -275.03) * mm, "end": v(-1031.83, -278.4) * mm});
            skArc(sketch, "E498.MirrorCS", {"start": v(-1037.5, -277.3) * mm, "mid": v(-1037.52, -275.05) * mm, "end": v(-1035.27, -275.03) * mm});
            skArc(sketch, "E499.MirrorCS", {"start": v(-1037.5, -277.3) * mm, "mid": v(-1037.02, -278.41) * mm, "end": v(-1037.47, -279.54) * mm});
            skLineSegment(sketch, "E500.trimOffspring", {"start": v(-1037.47, -279.54) * mm, "end": v(-1106.6, -349.96) * mm});
            skLineSegment(sketch, "E501", {"start": v(-1036.38, -276.16) * mm, "end": v(-1038.6, -278.43) * mm, "construction": true});
            skLineSegment(sketch, "E502", {"start": v(-1037.47, -279.54) * mm, "end": v(-1034.14, -276.14) * mm, "construction": true});
            skLineSegment(sketch, "E503", {"start": v(-1167.9, 795.17) * mm, "end": v(-1163.07, 795.17) * mm});
            skArc(sketch, "E504.MirrorCS", {"start": v(-1167.9, 792) * mm, "mid": v(-1169.48, 793.58) * mm, "end": v(-1167.9, 795.17) * mm});
            skArc(sketch, "E505.MirrorCS", {"start": v(-1167.9, 792) * mm, "mid": v(-1166.77, 791.53) * mm, "end": v(-1166.3, 790.4) * mm});
            skLineSegment(sketch, "E506.trimOffspring", {"start": v(-1166.3, 790.4) * mm, "end": v(-1166.3, 696.49) * mm});
            skLineSegment(sketch, "E507", {"start": v(-1167.9, 793.58) * mm, "end": v(-1167.9, 790.4) * mm, "construction": true});
            skLineSegment(sketch, "E508", {"start": v(-1166.3, 790.4) * mm, "end": v(-1166.3, 795.17) * mm, "construction": true});
            skLineSegment(sketch, "E509", {"start": v(-612.22, 827.8) * mm, "end": v(-607.39, 827.8) * mm});
            skArc(sketch, "E510.MirrorCS", {"start": v(-612.22, 824.62) * mm, "mid": v(-613.8, 826.21) * mm, "end": v(-612.22, 827.8) * mm});
            skArc(sketch, "E511.MirrorCS", {"start": v(-612.22, 824.62) * mm, "mid": v(-611.1, 824.16) * mm, "end": v(-610.63, 823.04) * mm});
            skLineSegment(sketch, "E512.trimOffspring", {"start": v(-610.63, 823.04) * mm, "end": v(-610.63, 729.12) * mm});
            skLineSegment(sketch, "E513", {"start": v(-612.22, 826.21) * mm, "end": v(-612.22, 823.04) * mm, "construction": true});
            skLineSegment(sketch, "E514", {"start": v(-610.63, 823.04) * mm, "end": v(-610.63, 827.8) * mm, "construction": true});
            skLineSegment(sketch, "E515", {"start": v(-1966.43, 808.4) * mm, "end": v(-1971.25, 808.4) * mm});
            skArc(sketch, "E516.MirrorCS", {"start": v(-1966.43, 811.57) * mm, "mid": v(-1964.84, 809.98) * mm, "end": v(-1966.43, 808.4) * mm});
            skArc(sketch, "E517.MirrorCS", {"start": v(-1966.43, 811.57) * mm, "mid": v(-1967.55, 812.03) * mm, "end": v(-1968.01, 813.15) * mm});
            skLineSegment(sketch, "E518.trimOffspring", {"start": v(-1968.01, 813.15) * mm, "end": v(-1968.01, 907.07) * mm});
            skLineSegment(sketch, "E519", {"start": v(-1966.43, 809.98) * mm, "end": v(-1966.43, 813.15) * mm, "construction": true});
            skLineSegment(sketch, "E520", {"start": v(-1968.01, 813.15) * mm, "end": v(-1968.01, 808.4) * mm, "construction": true});
            skPoint(sketch, "E521.orphan", {"position": v(-1971.25, 907.07) * mm});
            skLineSegment(sketch, "E522", {"start": v(-926.55, -357.63) * mm, "end": v(-1004.73, -297.41) * mm});
            skArc(sketch, "E523", {"start": v(-1005.02, -295.19) * mm, "mid": v(-1005.33, -296.36) * mm, "end": v(-1004.73, -297.41) * mm});
            skArc(sketch, "E524", {"start": v(-1005.02, -295.19) * mm, "mid": v(-1005.3, -292.96) * mm, "end": v(-1007.53, -293.25) * mm});
            skLineSegment(sketch, "E525", {"start": v(-1007.53, -293.25) * mm, "end": v(-1010.48, -297.07) * mm});
            skLineSegment(sketch, "E526", {"start": v(-1006.27, -294.22) * mm, "end": v(-1003.76, -296.16) * mm, "construction": true});
            skLineSegment(sketch, "E527", {"start": v(-1004.73, -297.41) * mm, "end": v(-1008.5, -294.5) * mm, "construction": true});
            skLineSegment(sketch, "E528", {"start": v(-1413.83, 696.49) * mm, "end": v(-1413.83, 790.4) * mm});
            skArc(sketch, "E529", {"start": v(-1412.24, 792) * mm, "mid": v(-1413.37, 791.53) * mm, "end": v(-1413.83, 790.4) * mm});
            skArc(sketch, "E530", {"start": v(-1412.24, 792) * mm, "mid": v(-1410.66, 793.58) * mm, "end": v(-1412.24, 795.17) * mm});
            skLineSegment(sketch, "E531", {"start": v(-1412.24, 795.17) * mm, "end": v(-1417.07, 795.17) * mm});
            skLineSegment(sketch, "E532", {"start": v(-1412.24, 793.58) * mm, "end": v(-1412.24, 790.4) * mm, "construction": true});
            skLineSegment(sketch, "E533", {"start": v(-1413.83, 790.4) * mm, "end": v(-1413.83, 795.17) * mm, "construction": true});
            skPoint(sketch, "E534.orphan", {"position": v(-1417.07, 696.49) * mm});
            skLineSegment(sketch, "E535", {"start": v(-1276.56, 469.45) * mm, "end": v(-1276.56, 375.53) * mm});
            skArc(sketch, "E536", {"start": v(-1278.14, 373.94) * mm, "mid": v(-1277.02, 374.4) * mm, "end": v(-1276.56, 375.53) * mm});
            skArc(sketch, "E537", {"start": v(-1278.14, 373.94) * mm, "mid": v(-1279.73, 372.36) * mm, "end": v(-1278.14, 370.77) * mm});
            skLineSegment(sketch, "E538", {"start": v(-1278.14, 370.77) * mm, "end": v(-1273.32, 370.77) * mm});
            skLineSegment(sketch, "E539", {"start": v(-1278.14, 372.36) * mm, "end": v(-1278.14, 375.53) * mm, "construction": true});
            skLineSegment(sketch, "E540", {"start": v(-1276.56, 375.53) * mm, "end": v(-1276.56, 370.77) * mm, "construction": true});
            skLineSegment(sketch, "E541", {"start": v(-1720.5, 907.07) * mm, "end": v(-1720.5, 813.15) * mm});
            skArc(sketch, "E542", {"start": v(-1722.08, 811.57) * mm, "mid": v(-1720.96, 812.03) * mm, "end": v(-1720.5, 813.15) * mm});
            skArc(sketch, "E543", {"start": v(-1722.08, 811.57) * mm, "mid": v(-1723.67, 809.98) * mm, "end": v(-1722.08, 808.4) * mm});
            skLineSegment(sketch, "E544", {"start": v(-1722.08, 808.4) * mm, "end": v(-1717.25, 808.4) * mm});
            skLineSegment(sketch, "E545", {"start": v(-1722.08, 809.98) * mm, "end": v(-1722.08, 813.15) * mm, "construction": true});
            skLineSegment(sketch, "E546", {"start": v(-1720.5, 813.15) * mm, "end": v(-1720.5, 808.4) * mm, "construction": true});
            skLineSegment(sketch, "E547", {"start": v(-1311.42, 310.7) * mm, "end": v(-1273.32, 310.7) * mm, "construction": true});
            skLineSegment(sketch, "E548", {"start": v(-1311.42, 310.7) * mm, "end": v(-1311.42, 272.6) * mm, "construction": true});
            skLineSegment(sketch, "E549", {"start": v(-1755.35, 748.32) * mm, "end": v(-1717.25, 748.32) * mm, "construction": true});
            skLineSegment(sketch, "E550", {"start": v(-1755.35, 748.32) * mm, "end": v(-1755.35, 710.22) * mm, "construction": true});
            skLineSegment(sketch, "E551", {"start": v(-645.49, 887.87) * mm, "end": v(-607.39, 887.87) * mm, "construction": true});
            skLineSegment(sketch, "E552", {"start": v(-645.49, 887.87) * mm, "end": v(-645.49, 925.97) * mm, "construction": true});
            skLineSegment(sketch, "E553", {"start": v(-1201.17, 855.24) * mm, "end": v(-1163.07, 855.24) * mm, "construction": true});
            skLineSegment(sketch, "E554", {"start": v(-1201.17, 855.24) * mm, "end": v(-1201.17, 893.34) * mm, "construction": true});
            skSolve(sketch);
        }
        {
            var Q0;
            {var subQ15=sQuery(id+"F2.wireOp",EDGE,"E130.bottom");Q0=makeQuery(id+"F2.imprint","IMPRINT",FACE,{"disambiguationData":[TD([[makeQuery(id+"F2.imprint","IMPRINT",EDGE,{"derivedFrom":subQ15}),-1.0]])]});}
            var Q1;
            {var subQ15=sQuery(id+"F2.wireOp",EDGE,"E211.bottom");Q1=makeQuery(id+"F2.imprint","IMPRINT",FACE,{"disambiguationData":[TD([[makeQuery(id+"F2.imprint","IMPRINT",EDGE,{"derivedFrom":subQ15}),-1.0]])]});}
            var Q2;
            Q2=makeQuery(id+"F2.imprint","IMPRINT",FACE,{"disambiguationData":[TD([[makeQuery(id+"F2.imprint","IMPRINT",EDGE,{"derivedFrom":sQuery(id+"F2.wireOp",EDGE,"E31.bottom")}),-1.0]])]});
            extrude(context, id + "F3", {"entities" : qUnion([Q0, Q1, Q2]), "depth" : (getVariable(context, 'TopPlateThickness')) * mm});
        }
        {
            var Q0;
            Q0=makeQuery(id+"F2.imprint","IMPRINT",FACE,{"disambiguationData":[TD([[makeQuery(id+"F2.imprint","IMPRINT",EDGE,{"derivedFrom":sQuery(id+"F2.wireOp",EDGE,"E459.bottom")}),-1.0]])]});
            var Q1;
            Q1=makeQuery(id+"F2.imprint","IMPRINT",FACE,{"disambiguationData":[TD([[makeQuery(id+"F2.imprint","IMPRINT",EDGE,{"derivedFrom":sQuery(id+"F2.wireOp",EDGE,"E388.bottom")}),-1.0]])]});
            var Q2;
            Q2=makeQuery(id+"F2.imprint","IMPRINT",FACE,{"disambiguationData":[TD([[makeQuery(id+"F2.imprint","IMPRINT",EDGE,{"derivedFrom":sQuery(id+"F2.wireOp",EDGE,"E352.bottom")}),-1.0]])]});
            var Q3;
            Q3=makeQuery(id+"F2.imprint","IMPRINT",FACE,{"disambiguationData":[TD([[makeQuery(id+"F2.imprint","IMPRINT",EDGE,{"derivedFrom":sQuery(id+"F2.wireOp",EDGE,"E281.bottom")}),-1.0]])]});
            extrude(context, id + "F4", {"entities" : qUnion([Q0, Q1, Q2, Q3]), "depth" : (getVariable(context, 'XMemberThickness')) * mm});
        }
    });
